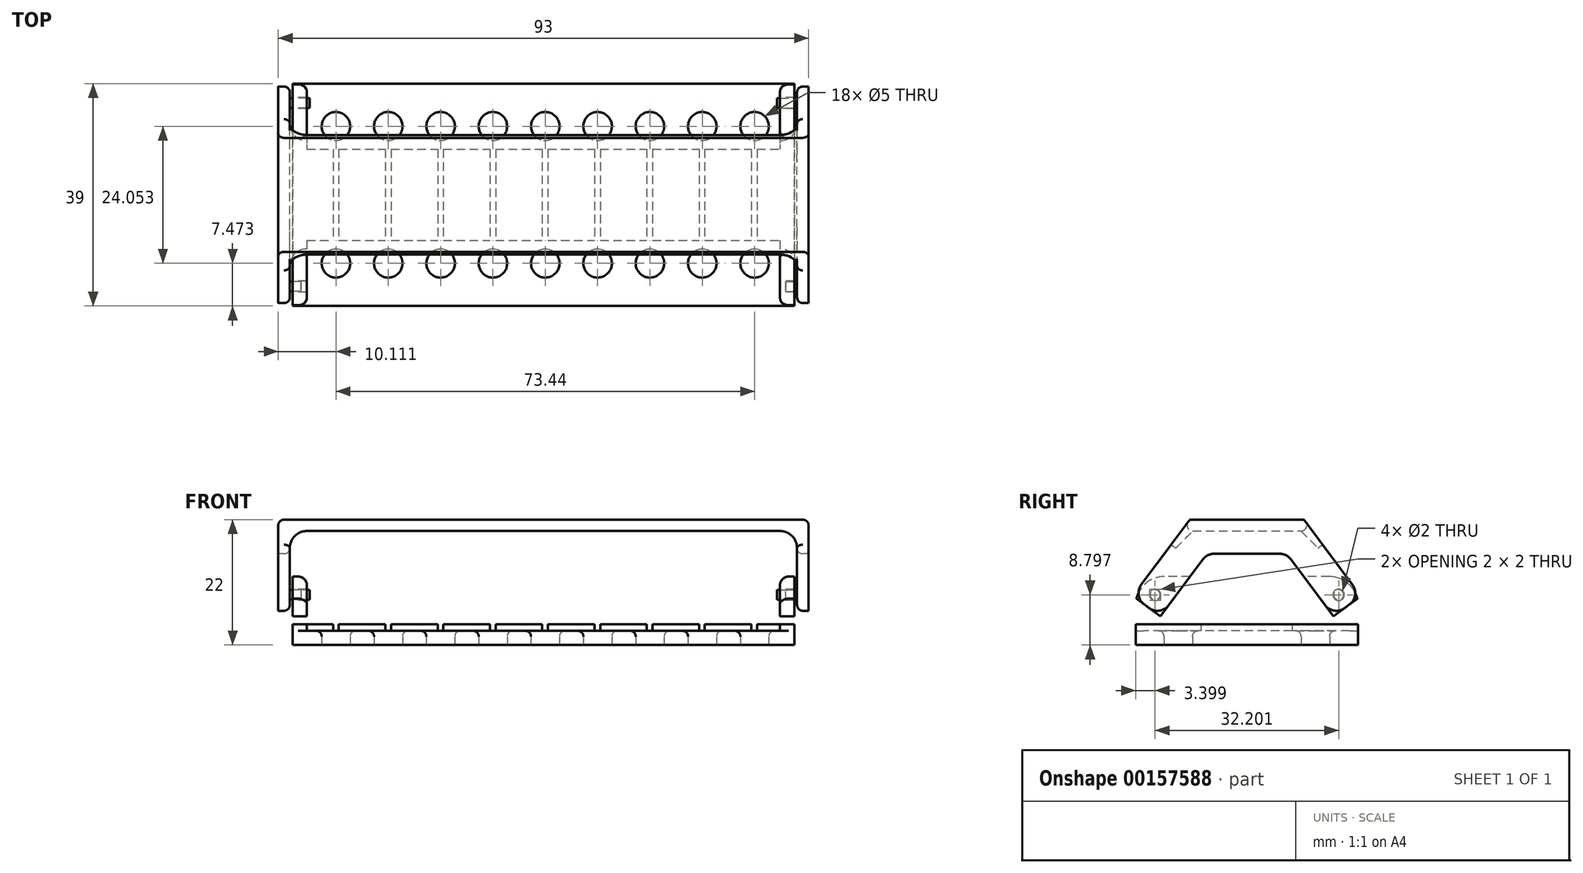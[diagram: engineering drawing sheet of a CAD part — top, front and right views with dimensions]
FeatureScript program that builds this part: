
annotation { "Feature Type Name" : "Feature", "Feature Type Description" : "" }
export const myFeature = defineFeature(function(context is Context, id is Id, definition is map)
    precondition{}
    {
        {
            var Q0;
            Q0=qCreatedBy(makeId("Top.planeOp"),FACE);
            var sketch = newSketch(context, id + "F0", { "sketchPlane" : qUnion([Q0])});
            skLineSegment(sketch, "E0.bottom", {"start": v(-44, 19.5) * mm, "end": v(44, 19.5) * mm});
            skLineSegment(sketch, "E0.top", {"start": v(-44, -19.5) * mm, "end": v(44, -19.5) * mm});
            skLineSegment(sketch, "E0.left", {"start": v(-44, 19.5) * mm, "end": v(-44, -19.5) * mm});
            skLineSegment(sketch, "E0.right", {"start": v(44, 19.5) * mm, "end": v(44, -19.5) * mm});
            skLineSegment(sketch, "E1", {"start": v(-44, 0) * mm, "end": v(44, 0) * mm, "construction": true});
            skSolve(sketch);
        }
        {
            var Q0;
            Q0=makeQuery(id+"F0.imprint","IMPRINT",FACE,{"disambiguationData":[TD([[makeQuery(id+"F0.imprint","IMPRINT",EDGE,{"derivedFrom":sQuery(id+"F0.wireOp",EDGE,"E0.bottom")}),-1.0]])]});
            var Q1;
            Q1=sQuery(id+"F0.wireOp",EDGE,"E0.top");
            extrude(context, id + "F1", {"entities" : qUnion([Q0]), "surfaceEntities" : qUnion([Q1]), "depth" : 12 * mm});
        }
        {
            var Q0;
            Q0=qCreatedBy(makeId("Top.planeOp"),FACE);
            cPlane(context, id + "F2", {"entities" : qUnion([Q0]), "cplaneType" : CPlaneType.OFFSET, "offset" : 12 * mm, "width" : 150 * mm, "height" : 150 * mm});
        }
        {
            var Q0;
            Q0=qCreatedBy(id+"F2.planeOp",FACE);
            var sketch = newSketch(context, id + "F3", { "sketchPlane" : qUnion([Q0])});
            skLineSegment(sketch, "E2.bottom", {"start": v(-41.5, 19.5) * mm, "end": v(41.5, 19.5) * mm});
            skLineSegment(sketch, "E2.top", {"start": v(-41.5, 8) * mm, "end": v(41.5, 8) * mm});
            skLineSegment(sketch, "E2.left", {"start": v(-41.5, 19.5) * mm, "end": v(-41.5, 8) * mm});
            skLineSegment(sketch, "E2.right", {"start": v(41.5, 19.5) * mm, "end": v(41.5, 8) * mm});
            skLineSegment(sketch, "E3.bottom", {"start": v(-41.5, -8) * mm, "end": v(41.5, -8) * mm});
            skLineSegment(sketch, "E3.top", {"start": v(-41.5, -19.5) * mm, "end": v(41.5, -19.5) * mm});
            skLineSegment(sketch, "E3.left", {"start": v(-41.5, -8) * mm, "end": v(-41.5, -19.5) * mm});
            skLineSegment(sketch, "E3.right", {"start": v(41.5, -8) * mm, "end": v(41.5, -19.5) * mm});
            skLineSegment(sketch, "E4", {"start": v(0, 8) * mm, "end": v(0, -8) * mm, "construction": true});
            skSolve(sketch);
        }
        {
            var Q0;
            Q0 = qSketchRegion(id + "F3", true);
            extrude(context, id + "F4", {"entities" : qUnion([Q0]), "operationType" : NewBodyOperationType.REMOVE, "oppositeDirection" : true, "depth" : 9.5 * mm});
        }
        {
            var Q0;
            Q0=qCreatedBy(id+"F2.planeOp",FACE);
            var sketch = newSketch(context, id + "F5", { "sketchPlane" : qUnion([Q0])});
            skLineSegment(sketch, "E5.bottom", {"start": v(-36.89, 8) * mm, "end": v(-35.89, 8) * mm});
            skLineSegment(sketch, "E5.top", {"start": v(-36.89, -8) * mm, "end": v(-35.89, -8) * mm});
            skLineSegment(sketch, "E5.left", {"start": v(-36.89, 8) * mm, "end": v(-36.89, -8) * mm});
            skLineSegment(sketch, "E5.right", {"start": v(-35.89, 8) * mm, "end": v(-35.89, -8) * mm});
            skLineSegment(sketch, "E6.1.0.0", {"start": v(-27.72, 8) * mm, "end": v(-26.72, 8) * mm});
            skLineSegment(sketch, "E6.1.0.1", {"start": v(-26.72, 8) * mm, "end": v(-26.72, -8) * mm});
            skLineSegment(sketch, "E6.1.0.2", {"start": v(-27.72, -8) * mm, "end": v(-26.72, -8) * mm});
            skLineSegment(sketch, "E6.1.0.3", {"start": v(-27.72, 8) * mm, "end": v(-27.72, -8) * mm});
            skLineSegment(sketch, "E6.2.0.0", {"start": v(-18.55, 8) * mm, "end": v(-17.55, 8) * mm});
            skLineSegment(sketch, "E6.2.0.1", {"start": v(-17.55, 8) * mm, "end": v(-17.55, -8) * mm});
            skLineSegment(sketch, "E6.2.0.2", {"start": v(-18.55, -8) * mm, "end": v(-17.55, -8) * mm});
            skLineSegment(sketch, "E6.2.0.3", {"start": v(-18.55, 8) * mm, "end": v(-18.55, -8) * mm});
            skLineSegment(sketch, "E6.3.0.0", {"start": v(-9.38, 8) * mm, "end": v(-8.38, 8) * mm});
            skLineSegment(sketch, "E6.3.0.1", {"start": v(-8.38, 8) * mm, "end": v(-8.38, -8) * mm});
            skLineSegment(sketch, "E6.3.0.2", {"start": v(-9.38, -8) * mm, "end": v(-8.38, -8) * mm});
            skLineSegment(sketch, "E6.3.0.3", {"start": v(-9.38, 8) * mm, "end": v(-9.38, -8) * mm});
            skLineSegment(sketch, "E6.4.0.0", {"start": v(-0.2, 8) * mm, "end": v(0.8, 8) * mm});
            skLineSegment(sketch, "E6.4.0.1", {"start": v(0.8, 8) * mm, "end": v(0.8, -8) * mm});
            skLineSegment(sketch, "E6.4.0.2", {"start": v(-0.2, -8) * mm, "end": v(0.8, -8) * mm});
            skLineSegment(sketch, "E6.4.0.3", {"start": v(-0.2, 8) * mm, "end": v(-0.2, -8) * mm});
            skLineSegment(sketch, "E6.5.0.0", {"start": v(8.96, 8) * mm, "end": v(9.96, 8) * mm});
            skLineSegment(sketch, "E6.5.0.1", {"start": v(9.96, 8) * mm, "end": v(9.96, -8) * mm});
            skLineSegment(sketch, "E6.5.0.2", {"start": v(8.96, -8) * mm, "end": v(9.96, -8) * mm});
            skLineSegment(sketch, "E6.5.0.3", {"start": v(8.96, 8) * mm, "end": v(8.96, -8) * mm});
            skLineSegment(sketch, "E6.6.0.0", {"start": v(18.13, 8) * mm, "end": v(19.13, 8) * mm});
            skLineSegment(sketch, "E6.6.0.1", {"start": v(19.13, 8) * mm, "end": v(19.13, -8) * mm});
            skLineSegment(sketch, "E6.6.0.2", {"start": v(18.13, -8) * mm, "end": v(19.13, -8) * mm});
            skLineSegment(sketch, "E6.6.0.3", {"start": v(18.13, 8) * mm, "end": v(18.13, -8) * mm});
            skLineSegment(sketch, "E6.7.0.0", {"start": v(27.3, 8) * mm, "end": v(28.3, 8) * mm});
            skLineSegment(sketch, "E6.7.0.1", {"start": v(28.3, 8) * mm, "end": v(28.3, -8) * mm});
            skLineSegment(sketch, "E6.7.0.2", {"start": v(27.3, -8) * mm, "end": v(28.3, -8) * mm});
            skLineSegment(sketch, "E6.7.0.3", {"start": v(27.3, 8) * mm, "end": v(27.3, -8) * mm});
            skLineSegment(sketch, "E6.8.0.0", {"start": v(36.47, 8) * mm, "end": v(37.47, 8) * mm});
            skLineSegment(sketch, "E6.8.0.1", {"start": v(37.47, 8) * mm, "end": v(37.47, -8) * mm});
            skLineSegment(sketch, "E6.8.0.2", {"start": v(36.47, -8) * mm, "end": v(37.47, -8) * mm});
            skLineSegment(sketch, "E6.8.0.3", {"start": v(36.47, 8) * mm, "end": v(36.47, -8) * mm});
            skLineSegment(sketch, "E6.direction1", {"start": v(-36.89, 8) * mm, "end": v(-27.72, 8) * mm, "construction": true});
            skSolve(sketch);
        }
        {
            var Q0;
            Q0=qCreatedBy(id+"F2.planeOp",FACE);
            var sketch = newSketch(context, id + "F6", { "sketchPlane" : qUnion([Q0])});
            skLineSegment(sketch, "E7.bottom", {"start": v(-41.5, 8) * mm, "end": v(41.5, 8) * mm});
            skLineSegment(sketch, "E7.top", {"start": v(-41.5, -8) * mm, "end": v(41.5, -8) * mm});
            skLineSegment(sketch, "E7.left", {"start": v(-41.5, 8) * mm, "end": v(-41.5, -8) * mm});
            skLineSegment(sketch, "E7.right", {"start": v(41.5, 8) * mm, "end": v(41.5, -8) * mm});
            skSolve(sketch);
        }
        {
            var Q0;
            Q0 = qSketchRegion(id + "F6", true);
            extrude(context, id + "F7", {"entities" : qUnion([Q0]), "operationType" : NewBodyOperationType.REMOVE, "oppositeDirection" : true, "depth" : 2 * mm});
        }
        {
            var Q0;
            Q0 = qSketchRegion(id + "F5", true);
            extrude(context, id + "F8", {"entities" : qUnion([Q0]), "operationType" : NewBodyOperationType.REMOVE, "oppositeDirection" : true, "depth" : 9.5 * mm});
        }
        {
            var Q0;
            {var subQ0=sQuery(id+"F0.wireOp",EDGE,"E0.left");var subQ1=sQuery(id+"F0.wireOp",EDGE,"E0.top");Q0=makeQuery(id+"F4.boolean.opBoolean","SPLIT",EDGE,{"disambiguationData":[TD([makeQuery(id+"F1.opExtrude","SWEPT_FACE",FACE,{"disambiguationData":[OSD([subQ0])]})])],"derivedFrom":makeQuery(id+"F1.opExtrude","CAP_EDGE",EDGE,{"disambiguationData":[OSD([subQ1])],"isStart":false})});}
            var Q1;
            {var subQ0=sQuery(id+"F0.wireOp",EDGE,"E0.bottom");var subQ1=sQuery(id+"F0.wireOp",EDGE,"E0.left");Q1=makeQuery(id+"F4.boolean.opBoolean","SPLIT",EDGE,{"disambiguationData":[TD([makeQuery(id+"F1.opExtrude","SWEPT_FACE",FACE,{"disambiguationData":[OSD([subQ1])]})])],"derivedFrom":makeQuery(id+"F1.opExtrude","CAP_EDGE",EDGE,{"disambiguationData":[OSD([subQ0])],"isStart":false})});}
            var Q2;
            {var subQ0=sQuery(id+"F0.wireOp",EDGE,"E0.right");var subQ1=sQuery(id+"F0.wireOp",EDGE,"E0.top");Q2=makeQuery(id+"F4.boolean.opBoolean","SPLIT",EDGE,{"disambiguationData":[TD([makeQuery(id+"F1.opExtrude","SWEPT_FACE",FACE,{"disambiguationData":[OSD([subQ0])]})])],"derivedFrom":makeQuery(id+"F1.opExtrude","CAP_EDGE",EDGE,{"disambiguationData":[OSD([subQ1])],"isStart":false})});}
            var Q3;
            {var subQ0=sQuery(id+"F0.wireOp",EDGE,"E0.bottom");var subQ1=sQuery(id+"F0.wireOp",EDGE,"E0.right");Q3=makeQuery(id+"F4.boolean.opBoolean","SPLIT",EDGE,{"disambiguationData":[TD([makeQuery(id+"F1.opExtrude","SWEPT_FACE",FACE,{"disambiguationData":[OSD([subQ1])]})])],"derivedFrom":makeQuery(id+"F1.opExtrude","CAP_EDGE",EDGE,{"disambiguationData":[OSD([subQ0])],"isStart":false})});}
            fillet(context, id + "F9", {"entities" : qUnion([Q0, Q1, Q2, Q3]), "radius" : 5 * mm, "tangentPropagation" : true, "allowEdgeOverflow" : false});
        }
        {
            var Q0;
            {var subQ0=makeQuery(id+"F4.opExtrude","SWEPT_FACE",FACE,{"disambiguationData":[OSD([sQuery(id+"F3.wireOp",EDGE,"E3.left")])]});var subQ1=sQuery(id+"F0.wireOp",EDGE,"E0.left");var subQ2=sQuery(id+"F0.wireOp",EDGE,"E0.top");Q0=makeQuery(id+"F9.opFillet","BLEND_EDGE",EDGE,{"blendedFrom":[makeQuery(id+"F4.boolean.opBoolean","SPLIT",EDGE,{"disambiguationData":[TD([makeQuery(id+"F1.opExtrude","SWEPT_FACE",FACE,{"disambiguationData":[OSD([subQ1])]})])],"derivedFrom":makeQuery(id+"F1.opExtrude","CAP_EDGE",EDGE,{"disambiguationData":[OSD([subQ2])],"isStart":false})}),makeQuery(id+"F7.boolean.opBoolean","MERGE",FACE,{"derivedFrom":[makeQuery(id+"F4.boolean.opBoolean","COPY",FACE,{"derivedFrom":makeQuery(id+"F4.opExtrude","SWEPT_FACE",FACE,{"disambiguationData":[OSD([sQuery(id+"F3.wireOp",EDGE,"E2.left")])]})}),makeQuery(id+"F4.boolean.opBoolean","COPY",FACE,{"derivedFrom":subQ0}),makeQuery(id+"F7.opExtrude","SWEPT_FACE",FACE,{"disambiguationData":[OSD([sQuery(id+"F6.wireOp",EDGE,"E7.left")])]})]})],"blendedInto":[makeQuery(id+"F7.boolean.opBoolean","MERGE",FACE,{"derivedFrom":[makeQuery(id+"F4.boolean.opBoolean","COPY",FACE,{"derivedFrom":makeQuery(id+"F4.opExtrude","SWEPT_FACE",FACE,{"disambiguationData":[OSD([sQuery(id+"F3.wireOp",EDGE,"E2.left")])]})}),makeQuery(id+"F4.boolean.opBoolean","COPY",FACE,{"derivedFrom":subQ0}),makeQuery(id+"F7.opExtrude","SWEPT_FACE",FACE,{"disambiguationData":[OSD([sQuery(id+"F6.wireOp",EDGE,"E7.left")])]})]})]});}
            var Q1;
            Q1=makeQuery(id+"F4.boolean.opBoolean","COPY",EDGE,{"derivedFrom":makeQuery(id+"F4.opExtrude","CAP_EDGE",EDGE,{"disambiguationData":[OSD([sQuery(id+"F3.wireOp",EDGE,"E3.top")])],"isStart":false})});
            var Q2;
            {var subQ0=makeQuery(id+"F4.opExtrude","SWEPT_FACE",FACE,{"disambiguationData":[OSD([sQuery(id+"F3.wireOp",EDGE,"E3.right")])]});var subQ1=sQuery(id+"F0.wireOp",EDGE,"E0.right");var subQ2=sQuery(id+"F0.wireOp",EDGE,"E0.top");Q2=makeQuery(id+"F9.opFillet","BLEND_EDGE",EDGE,{"blendedFrom":[makeQuery(id+"F4.boolean.opBoolean","SPLIT",EDGE,{"disambiguationData":[TD([makeQuery(id+"F1.opExtrude","SWEPT_FACE",FACE,{"disambiguationData":[OSD([subQ1])]})])],"derivedFrom":makeQuery(id+"F1.opExtrude","CAP_EDGE",EDGE,{"disambiguationData":[OSD([subQ2])],"isStart":false})}),makeQuery(id+"F7.boolean.opBoolean","MERGE",FACE,{"derivedFrom":[makeQuery(id+"F4.boolean.opBoolean","COPY",FACE,{"derivedFrom":makeQuery(id+"F4.opExtrude","SWEPT_FACE",FACE,{"disambiguationData":[OSD([sQuery(id+"F3.wireOp",EDGE,"E2.right")])]})}),makeQuery(id+"F4.boolean.opBoolean","COPY",FACE,{"derivedFrom":subQ0}),makeQuery(id+"F7.opExtrude","SWEPT_FACE",FACE,{"disambiguationData":[OSD([sQuery(id+"F6.wireOp",EDGE,"E7.right")])]})]})],"blendedInto":[makeQuery(id+"F7.boolean.opBoolean","MERGE",FACE,{"derivedFrom":[makeQuery(id+"F4.boolean.opBoolean","COPY",FACE,{"derivedFrom":makeQuery(id+"F4.opExtrude","SWEPT_FACE",FACE,{"disambiguationData":[OSD([sQuery(id+"F3.wireOp",EDGE,"E2.right")])]})}),makeQuery(id+"F4.boolean.opBoolean","COPY",FACE,{"derivedFrom":subQ0}),makeQuery(id+"F7.opExtrude","SWEPT_FACE",FACE,{"disambiguationData":[OSD([sQuery(id+"F6.wireOp",EDGE,"E7.right")])]})]})]});}
            var Q3;
            Q3=makeQuery(id+"F4.boolean.opBoolean","COPY",EDGE,{"derivedFrom":makeQuery(id+"F4.opExtrude","CAP_EDGE",EDGE,{"disambiguationData":[OSD([sQuery(id+"F3.wireOp",EDGE,"E2.bottom")])],"isStart":false})});
            fillet(context, id + "F10", {"entities" : qUnion([Q0, Q1, Q2, Q3]), "radius" : 1.5 * mm, "tangentPropagation" : true, "allowEdgeOverflow" : false});
        }
        {
            var Q0;
            Q0=qCreatedBy(makeId("Top.planeOp"),FACE);
            var sketch = newSketch(context, id + "F11", { "sketchPlane" : qUnion([Q0])});
            skCircle(sketch, "E8", {"center": v(-36.39, 12.03) * mm, "radius": 2.5 * mm});
            skLineSegment(sketch, "E9", {"start": v(-36.39, 12.03) * mm, "end": v(-36.39, 7.94) * mm});
            skCircle(sketch, "E10.1.0.0", {"center": v(-27.2, 12.03) * mm, "radius": 2.5 * mm});
            skCircle(sketch, "E10.2.0.0", {"center": v(-18.03, 12.03) * mm, "radius": 2.5 * mm});
            skCircle(sketch, "E10.3.0.0", {"center": v(-8.85, 12.03) * mm, "radius": 2.5 * mm});
            skCircle(sketch, "E10.4.0.0", {"center": v(0.33, 12.03) * mm, "radius": 2.5 * mm});
            skCircle(sketch, "E10.5.0.0", {"center": v(9.51, 12.03) * mm, "radius": 2.5 * mm});
            skCircle(sketch, "E10.6.0.0", {"center": v(18.7, 12.03) * mm, "radius": 2.5 * mm});
            skCircle(sketch, "E10.7.0.0", {"center": v(27.87, 12.03) * mm, "radius": 2.5 * mm});
            skCircle(sketch, "E10.8.0.0", {"center": v(37.05, 12.03) * mm, "radius": 2.5 * mm});
            skLineSegment(sketch, "E10.direction1", {"start": v(-36.39, 12.03) * mm, "end": v(-27.2, 12.03) * mm, "construction": true});
            skLineSegment(sketch, "E11", {"start": v(-41.42, 0) * mm, "end": v(0, 0) * mm, "construction": true});
            skCircle(sketch, "E12.MirrorC", {"center": v(-36.39, -12.03) * mm, "radius": 2.5 * mm});
            skCircle(sketch, "E13.MirrorC", {"center": v(-27.2, -12.03) * mm, "radius": 2.5 * mm});
            skCircle(sketch, "E14.MirrorC", {"center": v(-18.03, -12.03) * mm, "radius": 2.5 * mm});
            skCircle(sketch, "E15.MirrorC", {"center": v(-8.85, -12.03) * mm, "radius": 2.5 * mm});
            skCircle(sketch, "E16.MirrorC", {"center": v(0.33, -12.03) * mm, "radius": 2.5 * mm});
            skCircle(sketch, "E17.MirrorC", {"center": v(9.51, -12.03) * mm, "radius": 2.5 * mm});
            skCircle(sketch, "E18.MirrorC", {"center": v(18.7, -12.03) * mm, "radius": 2.5 * mm});
            skCircle(sketch, "E19.MirrorC", {"center": v(27.87, -12.03) * mm, "radius": 2.5 * mm});
            skCircle(sketch, "E20.MirrorC", {"center": v(37.05, -12.03) * mm, "radius": 2.5 * mm});
            skSolve(sketch);
        }
        {
            var Q0;
            Q0 = qSketchRegion(id + "F11", true);
            extrude(context, id + "F12", {"entities" : qUnion([Q0]), "operationType" : NewBodyOperationType.REMOVE, "depth" : 25 * mm});
        }
        {
            var Q0;
            Q0=makeQuery(id+"F12.boolean.opBoolean","INTERSECT",EDGE,{"derivedFrom":[makeQuery(id+"F8.boolean.opBoolean","MERGE",FACE,{"derivedFrom":[makeQuery(id+"F4.boolean.opBoolean","COPY",FACE,{"derivedFrom":makeQuery(id+"F4.opExtrude","CAP_FACE",FACE,{"disambiguationData":[OSD([sQuery(id+"F3.wireOp",EDGE,"E2.bottom"),sQuery(id+"F3.wireOp",EDGE,"E2.top"),sQuery(id+"F3.wireOp",EDGE,"E2.left"),sQuery(id+"F3.wireOp",EDGE,"E2.right")])],"isStart":false})}),makeQuery(id+"F4.boolean.opBoolean","COPY",FACE,{"derivedFrom":makeQuery(id+"F4.opExtrude","CAP_FACE",FACE,{"disambiguationData":[OSD([sQuery(id+"F3.wireOp",EDGE,"E3.bottom"),sQuery(id+"F3.wireOp",EDGE,"E3.top"),sQuery(id+"F3.wireOp",EDGE,"E3.left"),sQuery(id+"F3.wireOp",EDGE,"E3.right")])],"isStart":false})}),makeQuery(id+"F8.opExtrude","CAP_FACE",FACE,{"disambiguationData":[OSD([sQuery(id+"F5.wireOp",EDGE,"E5.bottom"),sQuery(id+"F5.wireOp",EDGE,"E5.top"),sQuery(id+"F5.wireOp",EDGE,"E5.left"),sQuery(id+"F5.wireOp",EDGE,"E5.right")])],"isStart":false}),makeQuery(id+"F8.opExtrude","CAP_FACE",FACE,{"disambiguationData":[OSD([sQuery(id+"F5.wireOp",EDGE,"E6.1.0.0"),sQuery(id+"F5.wireOp",EDGE,"E6.1.0.1"),sQuery(id+"F5.wireOp",EDGE,"E6.1.0.2"),sQuery(id+"F5.wireOp",EDGE,"E6.1.0.3")])],"isStart":false}),makeQuery(id+"F8.opExtrude","CAP_FACE",FACE,{"disambiguationData":[OSD([sQuery(id+"F5.wireOp",EDGE,"E6.2.0.0"),sQuery(id+"F5.wireOp",EDGE,"E6.2.0.1"),sQuery(id+"F5.wireOp",EDGE,"E6.2.0.2"),sQuery(id+"F5.wireOp",EDGE,"E6.2.0.3")])],"isStart":false}),makeQuery(id+"F8.opExtrude","CAP_FACE",FACE,{"disambiguationData":[OSD([sQuery(id+"F5.wireOp",EDGE,"E6.3.0.0"),sQuery(id+"F5.wireOp",EDGE,"E6.3.0.1"),sQuery(id+"F5.wireOp",EDGE,"E6.3.0.2"),sQuery(id+"F5.wireOp",EDGE,"E6.3.0.3")])],"isStart":false}),makeQuery(id+"F8.opExtrude","CAP_FACE",FACE,{"disambiguationData":[OSD([sQuery(id+"F5.wireOp",EDGE,"E6.4.0.0"),sQuery(id+"F5.wireOp",EDGE,"E6.4.0.1"),sQuery(id+"F5.wireOp",EDGE,"E6.4.0.2"),sQuery(id+"F5.wireOp",EDGE,"E6.4.0.3")])],"isStart":false}),makeQuery(id+"F8.opExtrude","CAP_FACE",FACE,{"disambiguationData":[OSD([sQuery(id+"F5.wireOp",EDGE,"E6.5.0.0"),sQuery(id+"F5.wireOp",EDGE,"E6.5.0.1"),sQuery(id+"F5.wireOp",EDGE,"E6.5.0.2"),sQuery(id+"F5.wireOp",EDGE,"E6.5.0.3")])],"isStart":false}),makeQuery(id+"F8.opExtrude","CAP_FACE",FACE,{"disambiguationData":[OSD([sQuery(id+"F5.wireOp",EDGE,"E6.6.0.0"),sQuery(id+"F5.wireOp",EDGE,"E6.6.0.1"),sQuery(id+"F5.wireOp",EDGE,"E6.6.0.2"),sQuery(id+"F5.wireOp",EDGE,"E6.6.0.3")])],"isStart":false}),makeQuery(id+"F8.opExtrude","CAP_FACE",FACE,{"disambiguationData":[OSD([sQuery(id+"F5.wireOp",EDGE,"E6.7.0.0"),sQuery(id+"F5.wireOp",EDGE,"E6.7.0.1"),sQuery(id+"F5.wireOp",EDGE,"E6.7.0.2"),sQuery(id+"F5.wireOp",EDGE,"E6.7.0.3")])],"isStart":false}),makeQuery(id+"F8.opExtrude","CAP_FACE",FACE,{"disambiguationData":[OSD([sQuery(id+"F5.wireOp",EDGE,"E6.8.0.0"),sQuery(id+"F5.wireOp",EDGE,"E6.8.0.1"),sQuery(id+"F5.wireOp",EDGE,"E6.8.0.2"),sQuery(id+"F5.wireOp",EDGE,"E6.8.0.3")])],"isStart":false})]}),makeQuery(id+"F12.opExtrude","SWEPT_FACE",FACE,{"disambiguationData":[OSD([sQuery(id+"F11.wireOp",EDGE,"E12.MirrorC")])]})]});
            var Q1;
            Q1=makeQuery(id+"F12.boolean.opBoolean","INTERSECT",EDGE,{"derivedFrom":[makeQuery(id+"F8.boolean.opBoolean","MERGE",FACE,{"derivedFrom":[makeQuery(id+"F4.boolean.opBoolean","COPY",FACE,{"derivedFrom":makeQuery(id+"F4.opExtrude","CAP_FACE",FACE,{"disambiguationData":[OSD([sQuery(id+"F3.wireOp",EDGE,"E2.bottom"),sQuery(id+"F3.wireOp",EDGE,"E2.top"),sQuery(id+"F3.wireOp",EDGE,"E2.left"),sQuery(id+"F3.wireOp",EDGE,"E2.right")])],"isStart":false})}),makeQuery(id+"F4.boolean.opBoolean","COPY",FACE,{"derivedFrom":makeQuery(id+"F4.opExtrude","CAP_FACE",FACE,{"disambiguationData":[OSD([sQuery(id+"F3.wireOp",EDGE,"E3.bottom"),sQuery(id+"F3.wireOp",EDGE,"E3.top"),sQuery(id+"F3.wireOp",EDGE,"E3.left"),sQuery(id+"F3.wireOp",EDGE,"E3.right")])],"isStart":false})}),makeQuery(id+"F8.opExtrude","CAP_FACE",FACE,{"disambiguationData":[OSD([sQuery(id+"F5.wireOp",EDGE,"E5.bottom"),sQuery(id+"F5.wireOp",EDGE,"E5.top"),sQuery(id+"F5.wireOp",EDGE,"E5.left"),sQuery(id+"F5.wireOp",EDGE,"E5.right")])],"isStart":false}),makeQuery(id+"F8.opExtrude","CAP_FACE",FACE,{"disambiguationData":[OSD([sQuery(id+"F5.wireOp",EDGE,"E6.1.0.0"),sQuery(id+"F5.wireOp",EDGE,"E6.1.0.1"),sQuery(id+"F5.wireOp",EDGE,"E6.1.0.2"),sQuery(id+"F5.wireOp",EDGE,"E6.1.0.3")])],"isStart":false}),makeQuery(id+"F8.opExtrude","CAP_FACE",FACE,{"disambiguationData":[OSD([sQuery(id+"F5.wireOp",EDGE,"E6.2.0.0"),sQuery(id+"F5.wireOp",EDGE,"E6.2.0.1"),sQuery(id+"F5.wireOp",EDGE,"E6.2.0.2"),sQuery(id+"F5.wireOp",EDGE,"E6.2.0.3")])],"isStart":false}),makeQuery(id+"F8.opExtrude","CAP_FACE",FACE,{"disambiguationData":[OSD([sQuery(id+"F5.wireOp",EDGE,"E6.3.0.0"),sQuery(id+"F5.wireOp",EDGE,"E6.3.0.1"),sQuery(id+"F5.wireOp",EDGE,"E6.3.0.2"),sQuery(id+"F5.wireOp",EDGE,"E6.3.0.3")])],"isStart":false}),makeQuery(id+"F8.opExtrude","CAP_FACE",FACE,{"disambiguationData":[OSD([sQuery(id+"F5.wireOp",EDGE,"E6.4.0.0"),sQuery(id+"F5.wireOp",EDGE,"E6.4.0.1"),sQuery(id+"F5.wireOp",EDGE,"E6.4.0.2"),sQuery(id+"F5.wireOp",EDGE,"E6.4.0.3")])],"isStart":false}),makeQuery(id+"F8.opExtrude","CAP_FACE",FACE,{"disambiguationData":[OSD([sQuery(id+"F5.wireOp",EDGE,"E6.5.0.0"),sQuery(id+"F5.wireOp",EDGE,"E6.5.0.1"),sQuery(id+"F5.wireOp",EDGE,"E6.5.0.2"),sQuery(id+"F5.wireOp",EDGE,"E6.5.0.3")])],"isStart":false}),makeQuery(id+"F8.opExtrude","CAP_FACE",FACE,{"disambiguationData":[OSD([sQuery(id+"F5.wireOp",EDGE,"E6.6.0.0"),sQuery(id+"F5.wireOp",EDGE,"E6.6.0.1"),sQuery(id+"F5.wireOp",EDGE,"E6.6.0.2"),sQuery(id+"F5.wireOp",EDGE,"E6.6.0.3")])],"isStart":false}),makeQuery(id+"F8.opExtrude","CAP_FACE",FACE,{"disambiguationData":[OSD([sQuery(id+"F5.wireOp",EDGE,"E6.7.0.0"),sQuery(id+"F5.wireOp",EDGE,"E6.7.0.1"),sQuery(id+"F5.wireOp",EDGE,"E6.7.0.2"),sQuery(id+"F5.wireOp",EDGE,"E6.7.0.3")])],"isStart":false}),makeQuery(id+"F8.opExtrude","CAP_FACE",FACE,{"disambiguationData":[OSD([sQuery(id+"F5.wireOp",EDGE,"E6.8.0.0"),sQuery(id+"F5.wireOp",EDGE,"E6.8.0.1"),sQuery(id+"F5.wireOp",EDGE,"E6.8.0.2"),sQuery(id+"F5.wireOp",EDGE,"E6.8.0.3")])],"isStart":false})]}),makeQuery(id+"F12.opExtrude","SWEPT_FACE",FACE,{"disambiguationData":[OSD([sQuery(id+"F11.wireOp",EDGE,"E13.MirrorC")])]})]});
            var Q2;
            Q2=makeQuery(id+"F12.boolean.opBoolean","INTERSECT",EDGE,{"derivedFrom":[makeQuery(id+"F8.boolean.opBoolean","MERGE",FACE,{"derivedFrom":[makeQuery(id+"F4.boolean.opBoolean","COPY",FACE,{"derivedFrom":makeQuery(id+"F4.opExtrude","CAP_FACE",FACE,{"disambiguationData":[OSD([sQuery(id+"F3.wireOp",EDGE,"E2.bottom"),sQuery(id+"F3.wireOp",EDGE,"E2.top"),sQuery(id+"F3.wireOp",EDGE,"E2.left"),sQuery(id+"F3.wireOp",EDGE,"E2.right")])],"isStart":false})}),makeQuery(id+"F4.boolean.opBoolean","COPY",FACE,{"derivedFrom":makeQuery(id+"F4.opExtrude","CAP_FACE",FACE,{"disambiguationData":[OSD([sQuery(id+"F3.wireOp",EDGE,"E3.bottom"),sQuery(id+"F3.wireOp",EDGE,"E3.top"),sQuery(id+"F3.wireOp",EDGE,"E3.left"),sQuery(id+"F3.wireOp",EDGE,"E3.right")])],"isStart":false})}),makeQuery(id+"F8.opExtrude","CAP_FACE",FACE,{"disambiguationData":[OSD([sQuery(id+"F5.wireOp",EDGE,"E5.bottom"),sQuery(id+"F5.wireOp",EDGE,"E5.top"),sQuery(id+"F5.wireOp",EDGE,"E5.left"),sQuery(id+"F5.wireOp",EDGE,"E5.right")])],"isStart":false}),makeQuery(id+"F8.opExtrude","CAP_FACE",FACE,{"disambiguationData":[OSD([sQuery(id+"F5.wireOp",EDGE,"E6.1.0.0"),sQuery(id+"F5.wireOp",EDGE,"E6.1.0.1"),sQuery(id+"F5.wireOp",EDGE,"E6.1.0.2"),sQuery(id+"F5.wireOp",EDGE,"E6.1.0.3")])],"isStart":false}),makeQuery(id+"F8.opExtrude","CAP_FACE",FACE,{"disambiguationData":[OSD([sQuery(id+"F5.wireOp",EDGE,"E6.2.0.0"),sQuery(id+"F5.wireOp",EDGE,"E6.2.0.1"),sQuery(id+"F5.wireOp",EDGE,"E6.2.0.2"),sQuery(id+"F5.wireOp",EDGE,"E6.2.0.3")])],"isStart":false}),makeQuery(id+"F8.opExtrude","CAP_FACE",FACE,{"disambiguationData":[OSD([sQuery(id+"F5.wireOp",EDGE,"E6.3.0.0"),sQuery(id+"F5.wireOp",EDGE,"E6.3.0.1"),sQuery(id+"F5.wireOp",EDGE,"E6.3.0.2"),sQuery(id+"F5.wireOp",EDGE,"E6.3.0.3")])],"isStart":false}),makeQuery(id+"F8.opExtrude","CAP_FACE",FACE,{"disambiguationData":[OSD([sQuery(id+"F5.wireOp",EDGE,"E6.4.0.0"),sQuery(id+"F5.wireOp",EDGE,"E6.4.0.1"),sQuery(id+"F5.wireOp",EDGE,"E6.4.0.2"),sQuery(id+"F5.wireOp",EDGE,"E6.4.0.3")])],"isStart":false}),makeQuery(id+"F8.opExtrude","CAP_FACE",FACE,{"disambiguationData":[OSD([sQuery(id+"F5.wireOp",EDGE,"E6.5.0.0"),sQuery(id+"F5.wireOp",EDGE,"E6.5.0.1"),sQuery(id+"F5.wireOp",EDGE,"E6.5.0.2"),sQuery(id+"F5.wireOp",EDGE,"E6.5.0.3")])],"isStart":false}),makeQuery(id+"F8.opExtrude","CAP_FACE",FACE,{"disambiguationData":[OSD([sQuery(id+"F5.wireOp",EDGE,"E6.6.0.0"),sQuery(id+"F5.wireOp",EDGE,"E6.6.0.1"),sQuery(id+"F5.wireOp",EDGE,"E6.6.0.2"),sQuery(id+"F5.wireOp",EDGE,"E6.6.0.3")])],"isStart":false}),makeQuery(id+"F8.opExtrude","CAP_FACE",FACE,{"disambiguationData":[OSD([sQuery(id+"F5.wireOp",EDGE,"E6.7.0.0"),sQuery(id+"F5.wireOp",EDGE,"E6.7.0.1"),sQuery(id+"F5.wireOp",EDGE,"E6.7.0.2"),sQuery(id+"F5.wireOp",EDGE,"E6.7.0.3")])],"isStart":false}),makeQuery(id+"F8.opExtrude","CAP_FACE",FACE,{"disambiguationData":[OSD([sQuery(id+"F5.wireOp",EDGE,"E6.8.0.0"),sQuery(id+"F5.wireOp",EDGE,"E6.8.0.1"),sQuery(id+"F5.wireOp",EDGE,"E6.8.0.2"),sQuery(id+"F5.wireOp",EDGE,"E6.8.0.3")])],"isStart":false})]}),makeQuery(id+"F12.opExtrude","SWEPT_FACE",FACE,{"disambiguationData":[OSD([sQuery(id+"F11.wireOp",EDGE,"E14.MirrorC")])]})]});
            var Q3;
            Q3=makeQuery(id+"F12.boolean.opBoolean","INTERSECT",EDGE,{"derivedFrom":[makeQuery(id+"F8.boolean.opBoolean","MERGE",FACE,{"derivedFrom":[makeQuery(id+"F4.boolean.opBoolean","COPY",FACE,{"derivedFrom":makeQuery(id+"F4.opExtrude","CAP_FACE",FACE,{"disambiguationData":[OSD([sQuery(id+"F3.wireOp",EDGE,"E2.bottom"),sQuery(id+"F3.wireOp",EDGE,"E2.top"),sQuery(id+"F3.wireOp",EDGE,"E2.left"),sQuery(id+"F3.wireOp",EDGE,"E2.right")])],"isStart":false})}),makeQuery(id+"F4.boolean.opBoolean","COPY",FACE,{"derivedFrom":makeQuery(id+"F4.opExtrude","CAP_FACE",FACE,{"disambiguationData":[OSD([sQuery(id+"F3.wireOp",EDGE,"E3.bottom"),sQuery(id+"F3.wireOp",EDGE,"E3.top"),sQuery(id+"F3.wireOp",EDGE,"E3.left"),sQuery(id+"F3.wireOp",EDGE,"E3.right")])],"isStart":false})}),makeQuery(id+"F8.opExtrude","CAP_FACE",FACE,{"disambiguationData":[OSD([sQuery(id+"F5.wireOp",EDGE,"E5.bottom"),sQuery(id+"F5.wireOp",EDGE,"E5.top"),sQuery(id+"F5.wireOp",EDGE,"E5.left"),sQuery(id+"F5.wireOp",EDGE,"E5.right")])],"isStart":false}),makeQuery(id+"F8.opExtrude","CAP_FACE",FACE,{"disambiguationData":[OSD([sQuery(id+"F5.wireOp",EDGE,"E6.1.0.0"),sQuery(id+"F5.wireOp",EDGE,"E6.1.0.1"),sQuery(id+"F5.wireOp",EDGE,"E6.1.0.2"),sQuery(id+"F5.wireOp",EDGE,"E6.1.0.3")])],"isStart":false}),makeQuery(id+"F8.opExtrude","CAP_FACE",FACE,{"disambiguationData":[OSD([sQuery(id+"F5.wireOp",EDGE,"E6.2.0.0"),sQuery(id+"F5.wireOp",EDGE,"E6.2.0.1"),sQuery(id+"F5.wireOp",EDGE,"E6.2.0.2"),sQuery(id+"F5.wireOp",EDGE,"E6.2.0.3")])],"isStart":false}),makeQuery(id+"F8.opExtrude","CAP_FACE",FACE,{"disambiguationData":[OSD([sQuery(id+"F5.wireOp",EDGE,"E6.3.0.0"),sQuery(id+"F5.wireOp",EDGE,"E6.3.0.1"),sQuery(id+"F5.wireOp",EDGE,"E6.3.0.2"),sQuery(id+"F5.wireOp",EDGE,"E6.3.0.3")])],"isStart":false}),makeQuery(id+"F8.opExtrude","CAP_FACE",FACE,{"disambiguationData":[OSD([sQuery(id+"F5.wireOp",EDGE,"E6.4.0.0"),sQuery(id+"F5.wireOp",EDGE,"E6.4.0.1"),sQuery(id+"F5.wireOp",EDGE,"E6.4.0.2"),sQuery(id+"F5.wireOp",EDGE,"E6.4.0.3")])],"isStart":false}),makeQuery(id+"F8.opExtrude","CAP_FACE",FACE,{"disambiguationData":[OSD([sQuery(id+"F5.wireOp",EDGE,"E6.5.0.0"),sQuery(id+"F5.wireOp",EDGE,"E6.5.0.1"),sQuery(id+"F5.wireOp",EDGE,"E6.5.0.2"),sQuery(id+"F5.wireOp",EDGE,"E6.5.0.3")])],"isStart":false}),makeQuery(id+"F8.opExtrude","CAP_FACE",FACE,{"disambiguationData":[OSD([sQuery(id+"F5.wireOp",EDGE,"E6.6.0.0"),sQuery(id+"F5.wireOp",EDGE,"E6.6.0.1"),sQuery(id+"F5.wireOp",EDGE,"E6.6.0.2"),sQuery(id+"F5.wireOp",EDGE,"E6.6.0.3")])],"isStart":false}),makeQuery(id+"F8.opExtrude","CAP_FACE",FACE,{"disambiguationData":[OSD([sQuery(id+"F5.wireOp",EDGE,"E6.7.0.0"),sQuery(id+"F5.wireOp",EDGE,"E6.7.0.1"),sQuery(id+"F5.wireOp",EDGE,"E6.7.0.2"),sQuery(id+"F5.wireOp",EDGE,"E6.7.0.3")])],"isStart":false}),makeQuery(id+"F8.opExtrude","CAP_FACE",FACE,{"disambiguationData":[OSD([sQuery(id+"F5.wireOp",EDGE,"E6.8.0.0"),sQuery(id+"F5.wireOp",EDGE,"E6.8.0.1"),sQuery(id+"F5.wireOp",EDGE,"E6.8.0.2"),sQuery(id+"F5.wireOp",EDGE,"E6.8.0.3")])],"isStart":false})]}),makeQuery(id+"F12.opExtrude","SWEPT_FACE",FACE,{"disambiguationData":[OSD([sQuery(id+"F11.wireOp",EDGE,"E15.MirrorC")])]})]});
            var Q4;
            Q4=makeQuery(id+"F12.boolean.opBoolean","INTERSECT",EDGE,{"derivedFrom":[makeQuery(id+"F8.boolean.opBoolean","MERGE",FACE,{"derivedFrom":[makeQuery(id+"F4.boolean.opBoolean","COPY",FACE,{"derivedFrom":makeQuery(id+"F4.opExtrude","CAP_FACE",FACE,{"disambiguationData":[OSD([sQuery(id+"F3.wireOp",EDGE,"E2.bottom"),sQuery(id+"F3.wireOp",EDGE,"E2.top"),sQuery(id+"F3.wireOp",EDGE,"E2.left"),sQuery(id+"F3.wireOp",EDGE,"E2.right")])],"isStart":false})}),makeQuery(id+"F4.boolean.opBoolean","COPY",FACE,{"derivedFrom":makeQuery(id+"F4.opExtrude","CAP_FACE",FACE,{"disambiguationData":[OSD([sQuery(id+"F3.wireOp",EDGE,"E3.bottom"),sQuery(id+"F3.wireOp",EDGE,"E3.top"),sQuery(id+"F3.wireOp",EDGE,"E3.left"),sQuery(id+"F3.wireOp",EDGE,"E3.right")])],"isStart":false})}),makeQuery(id+"F8.opExtrude","CAP_FACE",FACE,{"disambiguationData":[OSD([sQuery(id+"F5.wireOp",EDGE,"E5.bottom"),sQuery(id+"F5.wireOp",EDGE,"E5.top"),sQuery(id+"F5.wireOp",EDGE,"E5.left"),sQuery(id+"F5.wireOp",EDGE,"E5.right")])],"isStart":false}),makeQuery(id+"F8.opExtrude","CAP_FACE",FACE,{"disambiguationData":[OSD([sQuery(id+"F5.wireOp",EDGE,"E6.1.0.0"),sQuery(id+"F5.wireOp",EDGE,"E6.1.0.1"),sQuery(id+"F5.wireOp",EDGE,"E6.1.0.2"),sQuery(id+"F5.wireOp",EDGE,"E6.1.0.3")])],"isStart":false}),makeQuery(id+"F8.opExtrude","CAP_FACE",FACE,{"disambiguationData":[OSD([sQuery(id+"F5.wireOp",EDGE,"E6.2.0.0"),sQuery(id+"F5.wireOp",EDGE,"E6.2.0.1"),sQuery(id+"F5.wireOp",EDGE,"E6.2.0.2"),sQuery(id+"F5.wireOp",EDGE,"E6.2.0.3")])],"isStart":false}),makeQuery(id+"F8.opExtrude","CAP_FACE",FACE,{"disambiguationData":[OSD([sQuery(id+"F5.wireOp",EDGE,"E6.3.0.0"),sQuery(id+"F5.wireOp",EDGE,"E6.3.0.1"),sQuery(id+"F5.wireOp",EDGE,"E6.3.0.2"),sQuery(id+"F5.wireOp",EDGE,"E6.3.0.3")])],"isStart":false}),makeQuery(id+"F8.opExtrude","CAP_FACE",FACE,{"disambiguationData":[OSD([sQuery(id+"F5.wireOp",EDGE,"E6.4.0.0"),sQuery(id+"F5.wireOp",EDGE,"E6.4.0.1"),sQuery(id+"F5.wireOp",EDGE,"E6.4.0.2"),sQuery(id+"F5.wireOp",EDGE,"E6.4.0.3")])],"isStart":false}),makeQuery(id+"F8.opExtrude","CAP_FACE",FACE,{"disambiguationData":[OSD([sQuery(id+"F5.wireOp",EDGE,"E6.5.0.0"),sQuery(id+"F5.wireOp",EDGE,"E6.5.0.1"),sQuery(id+"F5.wireOp",EDGE,"E6.5.0.2"),sQuery(id+"F5.wireOp",EDGE,"E6.5.0.3")])],"isStart":false}),makeQuery(id+"F8.opExtrude","CAP_FACE",FACE,{"disambiguationData":[OSD([sQuery(id+"F5.wireOp",EDGE,"E6.6.0.0"),sQuery(id+"F5.wireOp",EDGE,"E6.6.0.1"),sQuery(id+"F5.wireOp",EDGE,"E6.6.0.2"),sQuery(id+"F5.wireOp",EDGE,"E6.6.0.3")])],"isStart":false}),makeQuery(id+"F8.opExtrude","CAP_FACE",FACE,{"disambiguationData":[OSD([sQuery(id+"F5.wireOp",EDGE,"E6.7.0.0"),sQuery(id+"F5.wireOp",EDGE,"E6.7.0.1"),sQuery(id+"F5.wireOp",EDGE,"E6.7.0.2"),sQuery(id+"F5.wireOp",EDGE,"E6.7.0.3")])],"isStart":false}),makeQuery(id+"F8.opExtrude","CAP_FACE",FACE,{"disambiguationData":[OSD([sQuery(id+"F5.wireOp",EDGE,"E6.8.0.0"),sQuery(id+"F5.wireOp",EDGE,"E6.8.0.1"),sQuery(id+"F5.wireOp",EDGE,"E6.8.0.2"),sQuery(id+"F5.wireOp",EDGE,"E6.8.0.3")])],"isStart":false})]}),makeQuery(id+"F12.opExtrude","SWEPT_FACE",FACE,{"disambiguationData":[OSD([sQuery(id+"F11.wireOp",EDGE,"E16.MirrorC")])]})]});
            var Q5;
            Q5=makeQuery(id+"F12.boolean.opBoolean","INTERSECT",EDGE,{"derivedFrom":[makeQuery(id+"F8.boolean.opBoolean","MERGE",FACE,{"derivedFrom":[makeQuery(id+"F4.boolean.opBoolean","COPY",FACE,{"derivedFrom":makeQuery(id+"F4.opExtrude","CAP_FACE",FACE,{"disambiguationData":[OSD([sQuery(id+"F3.wireOp",EDGE,"E2.bottom"),sQuery(id+"F3.wireOp",EDGE,"E2.top"),sQuery(id+"F3.wireOp",EDGE,"E2.left"),sQuery(id+"F3.wireOp",EDGE,"E2.right")])],"isStart":false})}),makeQuery(id+"F4.boolean.opBoolean","COPY",FACE,{"derivedFrom":makeQuery(id+"F4.opExtrude","CAP_FACE",FACE,{"disambiguationData":[OSD([sQuery(id+"F3.wireOp",EDGE,"E3.bottom"),sQuery(id+"F3.wireOp",EDGE,"E3.top"),sQuery(id+"F3.wireOp",EDGE,"E3.left"),sQuery(id+"F3.wireOp",EDGE,"E3.right")])],"isStart":false})}),makeQuery(id+"F8.opExtrude","CAP_FACE",FACE,{"disambiguationData":[OSD([sQuery(id+"F5.wireOp",EDGE,"E5.bottom"),sQuery(id+"F5.wireOp",EDGE,"E5.top"),sQuery(id+"F5.wireOp",EDGE,"E5.left"),sQuery(id+"F5.wireOp",EDGE,"E5.right")])],"isStart":false}),makeQuery(id+"F8.opExtrude","CAP_FACE",FACE,{"disambiguationData":[OSD([sQuery(id+"F5.wireOp",EDGE,"E6.1.0.0"),sQuery(id+"F5.wireOp",EDGE,"E6.1.0.1"),sQuery(id+"F5.wireOp",EDGE,"E6.1.0.2"),sQuery(id+"F5.wireOp",EDGE,"E6.1.0.3")])],"isStart":false}),makeQuery(id+"F8.opExtrude","CAP_FACE",FACE,{"disambiguationData":[OSD([sQuery(id+"F5.wireOp",EDGE,"E6.2.0.0"),sQuery(id+"F5.wireOp",EDGE,"E6.2.0.1"),sQuery(id+"F5.wireOp",EDGE,"E6.2.0.2"),sQuery(id+"F5.wireOp",EDGE,"E6.2.0.3")])],"isStart":false}),makeQuery(id+"F8.opExtrude","CAP_FACE",FACE,{"disambiguationData":[OSD([sQuery(id+"F5.wireOp",EDGE,"E6.3.0.0"),sQuery(id+"F5.wireOp",EDGE,"E6.3.0.1"),sQuery(id+"F5.wireOp",EDGE,"E6.3.0.2"),sQuery(id+"F5.wireOp",EDGE,"E6.3.0.3")])],"isStart":false}),makeQuery(id+"F8.opExtrude","CAP_FACE",FACE,{"disambiguationData":[OSD([sQuery(id+"F5.wireOp",EDGE,"E6.4.0.0"),sQuery(id+"F5.wireOp",EDGE,"E6.4.0.1"),sQuery(id+"F5.wireOp",EDGE,"E6.4.0.2"),sQuery(id+"F5.wireOp",EDGE,"E6.4.0.3")])],"isStart":false}),makeQuery(id+"F8.opExtrude","CAP_FACE",FACE,{"disambiguationData":[OSD([sQuery(id+"F5.wireOp",EDGE,"E6.5.0.0"),sQuery(id+"F5.wireOp",EDGE,"E6.5.0.1"),sQuery(id+"F5.wireOp",EDGE,"E6.5.0.2"),sQuery(id+"F5.wireOp",EDGE,"E6.5.0.3")])],"isStart":false}),makeQuery(id+"F8.opExtrude","CAP_FACE",FACE,{"disambiguationData":[OSD([sQuery(id+"F5.wireOp",EDGE,"E6.6.0.0"),sQuery(id+"F5.wireOp",EDGE,"E6.6.0.1"),sQuery(id+"F5.wireOp",EDGE,"E6.6.0.2"),sQuery(id+"F5.wireOp",EDGE,"E6.6.0.3")])],"isStart":false}),makeQuery(id+"F8.opExtrude","CAP_FACE",FACE,{"disambiguationData":[OSD([sQuery(id+"F5.wireOp",EDGE,"E6.7.0.0"),sQuery(id+"F5.wireOp",EDGE,"E6.7.0.1"),sQuery(id+"F5.wireOp",EDGE,"E6.7.0.2"),sQuery(id+"F5.wireOp",EDGE,"E6.7.0.3")])],"isStart":false}),makeQuery(id+"F8.opExtrude","CAP_FACE",FACE,{"disambiguationData":[OSD([sQuery(id+"F5.wireOp",EDGE,"E6.8.0.0"),sQuery(id+"F5.wireOp",EDGE,"E6.8.0.1"),sQuery(id+"F5.wireOp",EDGE,"E6.8.0.2"),sQuery(id+"F5.wireOp",EDGE,"E6.8.0.3")])],"isStart":false})]}),makeQuery(id+"F12.opExtrude","SWEPT_FACE",FACE,{"disambiguationData":[OSD([sQuery(id+"F11.wireOp",EDGE,"E17.MirrorC")])]})]});
            var Q6;
            Q6=makeQuery(id+"F12.boolean.opBoolean","INTERSECT",EDGE,{"derivedFrom":[makeQuery(id+"F8.boolean.opBoolean","MERGE",FACE,{"derivedFrom":[makeQuery(id+"F4.boolean.opBoolean","COPY",FACE,{"derivedFrom":makeQuery(id+"F4.opExtrude","CAP_FACE",FACE,{"disambiguationData":[OSD([sQuery(id+"F3.wireOp",EDGE,"E2.bottom"),sQuery(id+"F3.wireOp",EDGE,"E2.top"),sQuery(id+"F3.wireOp",EDGE,"E2.left"),sQuery(id+"F3.wireOp",EDGE,"E2.right")])],"isStart":false})}),makeQuery(id+"F4.boolean.opBoolean","COPY",FACE,{"derivedFrom":makeQuery(id+"F4.opExtrude","CAP_FACE",FACE,{"disambiguationData":[OSD([sQuery(id+"F3.wireOp",EDGE,"E3.bottom"),sQuery(id+"F3.wireOp",EDGE,"E3.top"),sQuery(id+"F3.wireOp",EDGE,"E3.left"),sQuery(id+"F3.wireOp",EDGE,"E3.right")])],"isStart":false})}),makeQuery(id+"F8.opExtrude","CAP_FACE",FACE,{"disambiguationData":[OSD([sQuery(id+"F5.wireOp",EDGE,"E5.bottom"),sQuery(id+"F5.wireOp",EDGE,"E5.top"),sQuery(id+"F5.wireOp",EDGE,"E5.left"),sQuery(id+"F5.wireOp",EDGE,"E5.right")])],"isStart":false}),makeQuery(id+"F8.opExtrude","CAP_FACE",FACE,{"disambiguationData":[OSD([sQuery(id+"F5.wireOp",EDGE,"E6.1.0.0"),sQuery(id+"F5.wireOp",EDGE,"E6.1.0.1"),sQuery(id+"F5.wireOp",EDGE,"E6.1.0.2"),sQuery(id+"F5.wireOp",EDGE,"E6.1.0.3")])],"isStart":false}),makeQuery(id+"F8.opExtrude","CAP_FACE",FACE,{"disambiguationData":[OSD([sQuery(id+"F5.wireOp",EDGE,"E6.2.0.0"),sQuery(id+"F5.wireOp",EDGE,"E6.2.0.1"),sQuery(id+"F5.wireOp",EDGE,"E6.2.0.2"),sQuery(id+"F5.wireOp",EDGE,"E6.2.0.3")])],"isStart":false}),makeQuery(id+"F8.opExtrude","CAP_FACE",FACE,{"disambiguationData":[OSD([sQuery(id+"F5.wireOp",EDGE,"E6.3.0.0"),sQuery(id+"F5.wireOp",EDGE,"E6.3.0.1"),sQuery(id+"F5.wireOp",EDGE,"E6.3.0.2"),sQuery(id+"F5.wireOp",EDGE,"E6.3.0.3")])],"isStart":false}),makeQuery(id+"F8.opExtrude","CAP_FACE",FACE,{"disambiguationData":[OSD([sQuery(id+"F5.wireOp",EDGE,"E6.4.0.0"),sQuery(id+"F5.wireOp",EDGE,"E6.4.0.1"),sQuery(id+"F5.wireOp",EDGE,"E6.4.0.2"),sQuery(id+"F5.wireOp",EDGE,"E6.4.0.3")])],"isStart":false}),makeQuery(id+"F8.opExtrude","CAP_FACE",FACE,{"disambiguationData":[OSD([sQuery(id+"F5.wireOp",EDGE,"E6.5.0.0"),sQuery(id+"F5.wireOp",EDGE,"E6.5.0.1"),sQuery(id+"F5.wireOp",EDGE,"E6.5.0.2"),sQuery(id+"F5.wireOp",EDGE,"E6.5.0.3")])],"isStart":false}),makeQuery(id+"F8.opExtrude","CAP_FACE",FACE,{"disambiguationData":[OSD([sQuery(id+"F5.wireOp",EDGE,"E6.6.0.0"),sQuery(id+"F5.wireOp",EDGE,"E6.6.0.1"),sQuery(id+"F5.wireOp",EDGE,"E6.6.0.2"),sQuery(id+"F5.wireOp",EDGE,"E6.6.0.3")])],"isStart":false}),makeQuery(id+"F8.opExtrude","CAP_FACE",FACE,{"disambiguationData":[OSD([sQuery(id+"F5.wireOp",EDGE,"E6.7.0.0"),sQuery(id+"F5.wireOp",EDGE,"E6.7.0.1"),sQuery(id+"F5.wireOp",EDGE,"E6.7.0.2"),sQuery(id+"F5.wireOp",EDGE,"E6.7.0.3")])],"isStart":false}),makeQuery(id+"F8.opExtrude","CAP_FACE",FACE,{"disambiguationData":[OSD([sQuery(id+"F5.wireOp",EDGE,"E6.8.0.0"),sQuery(id+"F5.wireOp",EDGE,"E6.8.0.1"),sQuery(id+"F5.wireOp",EDGE,"E6.8.0.2"),sQuery(id+"F5.wireOp",EDGE,"E6.8.0.3")])],"isStart":false})]}),makeQuery(id+"F12.opExtrude","SWEPT_FACE",FACE,{"disambiguationData":[OSD([sQuery(id+"F11.wireOp",EDGE,"E18.MirrorC")])]})]});
            var Q7;
            Q7=makeQuery(id+"F12.boolean.opBoolean","INTERSECT",EDGE,{"derivedFrom":[makeQuery(id+"F8.boolean.opBoolean","MERGE",FACE,{"derivedFrom":[makeQuery(id+"F4.boolean.opBoolean","COPY",FACE,{"derivedFrom":makeQuery(id+"F4.opExtrude","CAP_FACE",FACE,{"disambiguationData":[OSD([sQuery(id+"F3.wireOp",EDGE,"E2.bottom"),sQuery(id+"F3.wireOp",EDGE,"E2.top"),sQuery(id+"F3.wireOp",EDGE,"E2.left"),sQuery(id+"F3.wireOp",EDGE,"E2.right")])],"isStart":false})}),makeQuery(id+"F4.boolean.opBoolean","COPY",FACE,{"derivedFrom":makeQuery(id+"F4.opExtrude","CAP_FACE",FACE,{"disambiguationData":[OSD([sQuery(id+"F3.wireOp",EDGE,"E3.bottom"),sQuery(id+"F3.wireOp",EDGE,"E3.top"),sQuery(id+"F3.wireOp",EDGE,"E3.left"),sQuery(id+"F3.wireOp",EDGE,"E3.right")])],"isStart":false})}),makeQuery(id+"F8.opExtrude","CAP_FACE",FACE,{"disambiguationData":[OSD([sQuery(id+"F5.wireOp",EDGE,"E5.bottom"),sQuery(id+"F5.wireOp",EDGE,"E5.top"),sQuery(id+"F5.wireOp",EDGE,"E5.left"),sQuery(id+"F5.wireOp",EDGE,"E5.right")])],"isStart":false}),makeQuery(id+"F8.opExtrude","CAP_FACE",FACE,{"disambiguationData":[OSD([sQuery(id+"F5.wireOp",EDGE,"E6.1.0.0"),sQuery(id+"F5.wireOp",EDGE,"E6.1.0.1"),sQuery(id+"F5.wireOp",EDGE,"E6.1.0.2"),sQuery(id+"F5.wireOp",EDGE,"E6.1.0.3")])],"isStart":false}),makeQuery(id+"F8.opExtrude","CAP_FACE",FACE,{"disambiguationData":[OSD([sQuery(id+"F5.wireOp",EDGE,"E6.2.0.0"),sQuery(id+"F5.wireOp",EDGE,"E6.2.0.1"),sQuery(id+"F5.wireOp",EDGE,"E6.2.0.2"),sQuery(id+"F5.wireOp",EDGE,"E6.2.0.3")])],"isStart":false}),makeQuery(id+"F8.opExtrude","CAP_FACE",FACE,{"disambiguationData":[OSD([sQuery(id+"F5.wireOp",EDGE,"E6.3.0.0"),sQuery(id+"F5.wireOp",EDGE,"E6.3.0.1"),sQuery(id+"F5.wireOp",EDGE,"E6.3.0.2"),sQuery(id+"F5.wireOp",EDGE,"E6.3.0.3")])],"isStart":false}),makeQuery(id+"F8.opExtrude","CAP_FACE",FACE,{"disambiguationData":[OSD([sQuery(id+"F5.wireOp",EDGE,"E6.4.0.0"),sQuery(id+"F5.wireOp",EDGE,"E6.4.0.1"),sQuery(id+"F5.wireOp",EDGE,"E6.4.0.2"),sQuery(id+"F5.wireOp",EDGE,"E6.4.0.3")])],"isStart":false}),makeQuery(id+"F8.opExtrude","CAP_FACE",FACE,{"disambiguationData":[OSD([sQuery(id+"F5.wireOp",EDGE,"E6.5.0.0"),sQuery(id+"F5.wireOp",EDGE,"E6.5.0.1"),sQuery(id+"F5.wireOp",EDGE,"E6.5.0.2"),sQuery(id+"F5.wireOp",EDGE,"E6.5.0.3")])],"isStart":false}),makeQuery(id+"F8.opExtrude","CAP_FACE",FACE,{"disambiguationData":[OSD([sQuery(id+"F5.wireOp",EDGE,"E6.6.0.0"),sQuery(id+"F5.wireOp",EDGE,"E6.6.0.1"),sQuery(id+"F5.wireOp",EDGE,"E6.6.0.2"),sQuery(id+"F5.wireOp",EDGE,"E6.6.0.3")])],"isStart":false}),makeQuery(id+"F8.opExtrude","CAP_FACE",FACE,{"disambiguationData":[OSD([sQuery(id+"F5.wireOp",EDGE,"E6.7.0.0"),sQuery(id+"F5.wireOp",EDGE,"E6.7.0.1"),sQuery(id+"F5.wireOp",EDGE,"E6.7.0.2"),sQuery(id+"F5.wireOp",EDGE,"E6.7.0.3")])],"isStart":false}),makeQuery(id+"F8.opExtrude","CAP_FACE",FACE,{"disambiguationData":[OSD([sQuery(id+"F5.wireOp",EDGE,"E6.8.0.0"),sQuery(id+"F5.wireOp",EDGE,"E6.8.0.1"),sQuery(id+"F5.wireOp",EDGE,"E6.8.0.2"),sQuery(id+"F5.wireOp",EDGE,"E6.8.0.3")])],"isStart":false})]}),makeQuery(id+"F12.opExtrude","SWEPT_FACE",FACE,{"disambiguationData":[OSD([sQuery(id+"F11.wireOp",EDGE,"E19.MirrorC")])]})]});
            var Q8;
            Q8=makeQuery(id+"F12.boolean.opBoolean","INTERSECT",EDGE,{"derivedFrom":[makeQuery(id+"F8.boolean.opBoolean","MERGE",FACE,{"derivedFrom":[makeQuery(id+"F4.boolean.opBoolean","COPY",FACE,{"derivedFrom":makeQuery(id+"F4.opExtrude","CAP_FACE",FACE,{"disambiguationData":[OSD([sQuery(id+"F3.wireOp",EDGE,"E2.bottom"),sQuery(id+"F3.wireOp",EDGE,"E2.top"),sQuery(id+"F3.wireOp",EDGE,"E2.left"),sQuery(id+"F3.wireOp",EDGE,"E2.right")])],"isStart":false})}),makeQuery(id+"F4.boolean.opBoolean","COPY",FACE,{"derivedFrom":makeQuery(id+"F4.opExtrude","CAP_FACE",FACE,{"disambiguationData":[OSD([sQuery(id+"F3.wireOp",EDGE,"E3.bottom"),sQuery(id+"F3.wireOp",EDGE,"E3.top"),sQuery(id+"F3.wireOp",EDGE,"E3.left"),sQuery(id+"F3.wireOp",EDGE,"E3.right")])],"isStart":false})}),makeQuery(id+"F8.opExtrude","CAP_FACE",FACE,{"disambiguationData":[OSD([sQuery(id+"F5.wireOp",EDGE,"E5.bottom"),sQuery(id+"F5.wireOp",EDGE,"E5.top"),sQuery(id+"F5.wireOp",EDGE,"E5.left"),sQuery(id+"F5.wireOp",EDGE,"E5.right")])],"isStart":false}),makeQuery(id+"F8.opExtrude","CAP_FACE",FACE,{"disambiguationData":[OSD([sQuery(id+"F5.wireOp",EDGE,"E6.1.0.0"),sQuery(id+"F5.wireOp",EDGE,"E6.1.0.1"),sQuery(id+"F5.wireOp",EDGE,"E6.1.0.2"),sQuery(id+"F5.wireOp",EDGE,"E6.1.0.3")])],"isStart":false}),makeQuery(id+"F8.opExtrude","CAP_FACE",FACE,{"disambiguationData":[OSD([sQuery(id+"F5.wireOp",EDGE,"E6.2.0.0"),sQuery(id+"F5.wireOp",EDGE,"E6.2.0.1"),sQuery(id+"F5.wireOp",EDGE,"E6.2.0.2"),sQuery(id+"F5.wireOp",EDGE,"E6.2.0.3")])],"isStart":false}),makeQuery(id+"F8.opExtrude","CAP_FACE",FACE,{"disambiguationData":[OSD([sQuery(id+"F5.wireOp",EDGE,"E6.3.0.0"),sQuery(id+"F5.wireOp",EDGE,"E6.3.0.1"),sQuery(id+"F5.wireOp",EDGE,"E6.3.0.2"),sQuery(id+"F5.wireOp",EDGE,"E6.3.0.3")])],"isStart":false}),makeQuery(id+"F8.opExtrude","CAP_FACE",FACE,{"disambiguationData":[OSD([sQuery(id+"F5.wireOp",EDGE,"E6.4.0.0"),sQuery(id+"F5.wireOp",EDGE,"E6.4.0.1"),sQuery(id+"F5.wireOp",EDGE,"E6.4.0.2"),sQuery(id+"F5.wireOp",EDGE,"E6.4.0.3")])],"isStart":false}),makeQuery(id+"F8.opExtrude","CAP_FACE",FACE,{"disambiguationData":[OSD([sQuery(id+"F5.wireOp",EDGE,"E6.5.0.0"),sQuery(id+"F5.wireOp",EDGE,"E6.5.0.1"),sQuery(id+"F5.wireOp",EDGE,"E6.5.0.2"),sQuery(id+"F5.wireOp",EDGE,"E6.5.0.3")])],"isStart":false}),makeQuery(id+"F8.opExtrude","CAP_FACE",FACE,{"disambiguationData":[OSD([sQuery(id+"F5.wireOp",EDGE,"E6.6.0.0"),sQuery(id+"F5.wireOp",EDGE,"E6.6.0.1"),sQuery(id+"F5.wireOp",EDGE,"E6.6.0.2"),sQuery(id+"F5.wireOp",EDGE,"E6.6.0.3")])],"isStart":false}),makeQuery(id+"F8.opExtrude","CAP_FACE",FACE,{"disambiguationData":[OSD([sQuery(id+"F5.wireOp",EDGE,"E6.7.0.0"),sQuery(id+"F5.wireOp",EDGE,"E6.7.0.1"),sQuery(id+"F5.wireOp",EDGE,"E6.7.0.2"),sQuery(id+"F5.wireOp",EDGE,"E6.7.0.3")])],"isStart":false}),makeQuery(id+"F8.opExtrude","CAP_FACE",FACE,{"disambiguationData":[OSD([sQuery(id+"F5.wireOp",EDGE,"E6.8.0.0"),sQuery(id+"F5.wireOp",EDGE,"E6.8.0.1"),sQuery(id+"F5.wireOp",EDGE,"E6.8.0.2"),sQuery(id+"F5.wireOp",EDGE,"E6.8.0.3")])],"isStart":false})]}),makeQuery(id+"F12.opExtrude","SWEPT_FACE",FACE,{"disambiguationData":[OSD([sQuery(id+"F11.wireOp",EDGE,"E20.MirrorC")])]})]});
            var Q9;
            Q9=makeQuery(id+"F12.boolean.opBoolean","INTERSECT",EDGE,{"derivedFrom":[makeQuery(id+"F8.boolean.opBoolean","MERGE",FACE,{"derivedFrom":[makeQuery(id+"F4.boolean.opBoolean","COPY",FACE,{"derivedFrom":makeQuery(id+"F4.opExtrude","CAP_FACE",FACE,{"disambiguationData":[OSD([sQuery(id+"F3.wireOp",EDGE,"E2.bottom"),sQuery(id+"F3.wireOp",EDGE,"E2.top"),sQuery(id+"F3.wireOp",EDGE,"E2.left"),sQuery(id+"F3.wireOp",EDGE,"E2.right")])],"isStart":false})}),makeQuery(id+"F4.boolean.opBoolean","COPY",FACE,{"derivedFrom":makeQuery(id+"F4.opExtrude","CAP_FACE",FACE,{"disambiguationData":[OSD([sQuery(id+"F3.wireOp",EDGE,"E3.bottom"),sQuery(id+"F3.wireOp",EDGE,"E3.top"),sQuery(id+"F3.wireOp",EDGE,"E3.left"),sQuery(id+"F3.wireOp",EDGE,"E3.right")])],"isStart":false})}),makeQuery(id+"F8.opExtrude","CAP_FACE",FACE,{"disambiguationData":[OSD([sQuery(id+"F5.wireOp",EDGE,"E5.bottom"),sQuery(id+"F5.wireOp",EDGE,"E5.top"),sQuery(id+"F5.wireOp",EDGE,"E5.left"),sQuery(id+"F5.wireOp",EDGE,"E5.right")])],"isStart":false}),makeQuery(id+"F8.opExtrude","CAP_FACE",FACE,{"disambiguationData":[OSD([sQuery(id+"F5.wireOp",EDGE,"E6.1.0.0"),sQuery(id+"F5.wireOp",EDGE,"E6.1.0.1"),sQuery(id+"F5.wireOp",EDGE,"E6.1.0.2"),sQuery(id+"F5.wireOp",EDGE,"E6.1.0.3")])],"isStart":false}),makeQuery(id+"F8.opExtrude","CAP_FACE",FACE,{"disambiguationData":[OSD([sQuery(id+"F5.wireOp",EDGE,"E6.2.0.0"),sQuery(id+"F5.wireOp",EDGE,"E6.2.0.1"),sQuery(id+"F5.wireOp",EDGE,"E6.2.0.2"),sQuery(id+"F5.wireOp",EDGE,"E6.2.0.3")])],"isStart":false}),makeQuery(id+"F8.opExtrude","CAP_FACE",FACE,{"disambiguationData":[OSD([sQuery(id+"F5.wireOp",EDGE,"E6.3.0.0"),sQuery(id+"F5.wireOp",EDGE,"E6.3.0.1"),sQuery(id+"F5.wireOp",EDGE,"E6.3.0.2"),sQuery(id+"F5.wireOp",EDGE,"E6.3.0.3")])],"isStart":false}),makeQuery(id+"F8.opExtrude","CAP_FACE",FACE,{"disambiguationData":[OSD([sQuery(id+"F5.wireOp",EDGE,"E6.4.0.0"),sQuery(id+"F5.wireOp",EDGE,"E6.4.0.1"),sQuery(id+"F5.wireOp",EDGE,"E6.4.0.2"),sQuery(id+"F5.wireOp",EDGE,"E6.4.0.3")])],"isStart":false}),makeQuery(id+"F8.opExtrude","CAP_FACE",FACE,{"disambiguationData":[OSD([sQuery(id+"F5.wireOp",EDGE,"E6.5.0.0"),sQuery(id+"F5.wireOp",EDGE,"E6.5.0.1"),sQuery(id+"F5.wireOp",EDGE,"E6.5.0.2"),sQuery(id+"F5.wireOp",EDGE,"E6.5.0.3")])],"isStart":false}),makeQuery(id+"F8.opExtrude","CAP_FACE",FACE,{"disambiguationData":[OSD([sQuery(id+"F5.wireOp",EDGE,"E6.6.0.0"),sQuery(id+"F5.wireOp",EDGE,"E6.6.0.1"),sQuery(id+"F5.wireOp",EDGE,"E6.6.0.2"),sQuery(id+"F5.wireOp",EDGE,"E6.6.0.3")])],"isStart":false}),makeQuery(id+"F8.opExtrude","CAP_FACE",FACE,{"disambiguationData":[OSD([sQuery(id+"F5.wireOp",EDGE,"E6.7.0.0"),sQuery(id+"F5.wireOp",EDGE,"E6.7.0.1"),sQuery(id+"F5.wireOp",EDGE,"E6.7.0.2"),sQuery(id+"F5.wireOp",EDGE,"E6.7.0.3")])],"isStart":false}),makeQuery(id+"F8.opExtrude","CAP_FACE",FACE,{"disambiguationData":[OSD([sQuery(id+"F5.wireOp",EDGE,"E6.8.0.0"),sQuery(id+"F5.wireOp",EDGE,"E6.8.0.1"),sQuery(id+"F5.wireOp",EDGE,"E6.8.0.2"),sQuery(id+"F5.wireOp",EDGE,"E6.8.0.3")])],"isStart":false})]}),makeQuery(id+"F12.opExtrude","SWEPT_FACE",FACE,{"disambiguationData":[OSD([sQuery(id+"F11.wireOp",EDGE,"E8")])]})]});
            var Q10;
            Q10=makeQuery(id+"F12.boolean.opBoolean","INTERSECT",EDGE,{"derivedFrom":[makeQuery(id+"F8.boolean.opBoolean","MERGE",FACE,{"derivedFrom":[makeQuery(id+"F4.boolean.opBoolean","COPY",FACE,{"derivedFrom":makeQuery(id+"F4.opExtrude","CAP_FACE",FACE,{"disambiguationData":[OSD([sQuery(id+"F3.wireOp",EDGE,"E2.bottom"),sQuery(id+"F3.wireOp",EDGE,"E2.top"),sQuery(id+"F3.wireOp",EDGE,"E2.left"),sQuery(id+"F3.wireOp",EDGE,"E2.right")])],"isStart":false})}),makeQuery(id+"F4.boolean.opBoolean","COPY",FACE,{"derivedFrom":makeQuery(id+"F4.opExtrude","CAP_FACE",FACE,{"disambiguationData":[OSD([sQuery(id+"F3.wireOp",EDGE,"E3.bottom"),sQuery(id+"F3.wireOp",EDGE,"E3.top"),sQuery(id+"F3.wireOp",EDGE,"E3.left"),sQuery(id+"F3.wireOp",EDGE,"E3.right")])],"isStart":false})}),makeQuery(id+"F8.opExtrude","CAP_FACE",FACE,{"disambiguationData":[OSD([sQuery(id+"F5.wireOp",EDGE,"E5.bottom"),sQuery(id+"F5.wireOp",EDGE,"E5.top"),sQuery(id+"F5.wireOp",EDGE,"E5.left"),sQuery(id+"F5.wireOp",EDGE,"E5.right")])],"isStart":false}),makeQuery(id+"F8.opExtrude","CAP_FACE",FACE,{"disambiguationData":[OSD([sQuery(id+"F5.wireOp",EDGE,"E6.1.0.0"),sQuery(id+"F5.wireOp",EDGE,"E6.1.0.1"),sQuery(id+"F5.wireOp",EDGE,"E6.1.0.2"),sQuery(id+"F5.wireOp",EDGE,"E6.1.0.3")])],"isStart":false}),makeQuery(id+"F8.opExtrude","CAP_FACE",FACE,{"disambiguationData":[OSD([sQuery(id+"F5.wireOp",EDGE,"E6.2.0.0"),sQuery(id+"F5.wireOp",EDGE,"E6.2.0.1"),sQuery(id+"F5.wireOp",EDGE,"E6.2.0.2"),sQuery(id+"F5.wireOp",EDGE,"E6.2.0.3")])],"isStart":false}),makeQuery(id+"F8.opExtrude","CAP_FACE",FACE,{"disambiguationData":[OSD([sQuery(id+"F5.wireOp",EDGE,"E6.3.0.0"),sQuery(id+"F5.wireOp",EDGE,"E6.3.0.1"),sQuery(id+"F5.wireOp",EDGE,"E6.3.0.2"),sQuery(id+"F5.wireOp",EDGE,"E6.3.0.3")])],"isStart":false}),makeQuery(id+"F8.opExtrude","CAP_FACE",FACE,{"disambiguationData":[OSD([sQuery(id+"F5.wireOp",EDGE,"E6.4.0.0"),sQuery(id+"F5.wireOp",EDGE,"E6.4.0.1"),sQuery(id+"F5.wireOp",EDGE,"E6.4.0.2"),sQuery(id+"F5.wireOp",EDGE,"E6.4.0.3")])],"isStart":false}),makeQuery(id+"F8.opExtrude","CAP_FACE",FACE,{"disambiguationData":[OSD([sQuery(id+"F5.wireOp",EDGE,"E6.5.0.0"),sQuery(id+"F5.wireOp",EDGE,"E6.5.0.1"),sQuery(id+"F5.wireOp",EDGE,"E6.5.0.2"),sQuery(id+"F5.wireOp",EDGE,"E6.5.0.3")])],"isStart":false}),makeQuery(id+"F8.opExtrude","CAP_FACE",FACE,{"disambiguationData":[OSD([sQuery(id+"F5.wireOp",EDGE,"E6.6.0.0"),sQuery(id+"F5.wireOp",EDGE,"E6.6.0.1"),sQuery(id+"F5.wireOp",EDGE,"E6.6.0.2"),sQuery(id+"F5.wireOp",EDGE,"E6.6.0.3")])],"isStart":false}),makeQuery(id+"F8.opExtrude","CAP_FACE",FACE,{"disambiguationData":[OSD([sQuery(id+"F5.wireOp",EDGE,"E6.7.0.0"),sQuery(id+"F5.wireOp",EDGE,"E6.7.0.1"),sQuery(id+"F5.wireOp",EDGE,"E6.7.0.2"),sQuery(id+"F5.wireOp",EDGE,"E6.7.0.3")])],"isStart":false}),makeQuery(id+"F8.opExtrude","CAP_FACE",FACE,{"disambiguationData":[OSD([sQuery(id+"F5.wireOp",EDGE,"E6.8.0.0"),sQuery(id+"F5.wireOp",EDGE,"E6.8.0.1"),sQuery(id+"F5.wireOp",EDGE,"E6.8.0.2"),sQuery(id+"F5.wireOp",EDGE,"E6.8.0.3")])],"isStart":false})]}),makeQuery(id+"F12.opExtrude","SWEPT_FACE",FACE,{"disambiguationData":[OSD([sQuery(id+"F11.wireOp",EDGE,"E10.1.0.0")])]})]});
            var Q11;
            Q11=makeQuery(id+"F12.boolean.opBoolean","INTERSECT",EDGE,{"derivedFrom":[makeQuery(id+"F8.boolean.opBoolean","MERGE",FACE,{"derivedFrom":[makeQuery(id+"F4.boolean.opBoolean","COPY",FACE,{"derivedFrom":makeQuery(id+"F4.opExtrude","CAP_FACE",FACE,{"disambiguationData":[OSD([sQuery(id+"F3.wireOp",EDGE,"E2.bottom"),sQuery(id+"F3.wireOp",EDGE,"E2.top"),sQuery(id+"F3.wireOp",EDGE,"E2.left"),sQuery(id+"F3.wireOp",EDGE,"E2.right")])],"isStart":false})}),makeQuery(id+"F4.boolean.opBoolean","COPY",FACE,{"derivedFrom":makeQuery(id+"F4.opExtrude","CAP_FACE",FACE,{"disambiguationData":[OSD([sQuery(id+"F3.wireOp",EDGE,"E3.bottom"),sQuery(id+"F3.wireOp",EDGE,"E3.top"),sQuery(id+"F3.wireOp",EDGE,"E3.left"),sQuery(id+"F3.wireOp",EDGE,"E3.right")])],"isStart":false})}),makeQuery(id+"F8.opExtrude","CAP_FACE",FACE,{"disambiguationData":[OSD([sQuery(id+"F5.wireOp",EDGE,"E5.bottom"),sQuery(id+"F5.wireOp",EDGE,"E5.top"),sQuery(id+"F5.wireOp",EDGE,"E5.left"),sQuery(id+"F5.wireOp",EDGE,"E5.right")])],"isStart":false}),makeQuery(id+"F8.opExtrude","CAP_FACE",FACE,{"disambiguationData":[OSD([sQuery(id+"F5.wireOp",EDGE,"E6.1.0.0"),sQuery(id+"F5.wireOp",EDGE,"E6.1.0.1"),sQuery(id+"F5.wireOp",EDGE,"E6.1.0.2"),sQuery(id+"F5.wireOp",EDGE,"E6.1.0.3")])],"isStart":false}),makeQuery(id+"F8.opExtrude","CAP_FACE",FACE,{"disambiguationData":[OSD([sQuery(id+"F5.wireOp",EDGE,"E6.2.0.0"),sQuery(id+"F5.wireOp",EDGE,"E6.2.0.1"),sQuery(id+"F5.wireOp",EDGE,"E6.2.0.2"),sQuery(id+"F5.wireOp",EDGE,"E6.2.0.3")])],"isStart":false}),makeQuery(id+"F8.opExtrude","CAP_FACE",FACE,{"disambiguationData":[OSD([sQuery(id+"F5.wireOp",EDGE,"E6.3.0.0"),sQuery(id+"F5.wireOp",EDGE,"E6.3.0.1"),sQuery(id+"F5.wireOp",EDGE,"E6.3.0.2"),sQuery(id+"F5.wireOp",EDGE,"E6.3.0.3")])],"isStart":false}),makeQuery(id+"F8.opExtrude","CAP_FACE",FACE,{"disambiguationData":[OSD([sQuery(id+"F5.wireOp",EDGE,"E6.4.0.0"),sQuery(id+"F5.wireOp",EDGE,"E6.4.0.1"),sQuery(id+"F5.wireOp",EDGE,"E6.4.0.2"),sQuery(id+"F5.wireOp",EDGE,"E6.4.0.3")])],"isStart":false}),makeQuery(id+"F8.opExtrude","CAP_FACE",FACE,{"disambiguationData":[OSD([sQuery(id+"F5.wireOp",EDGE,"E6.5.0.0"),sQuery(id+"F5.wireOp",EDGE,"E6.5.0.1"),sQuery(id+"F5.wireOp",EDGE,"E6.5.0.2"),sQuery(id+"F5.wireOp",EDGE,"E6.5.0.3")])],"isStart":false}),makeQuery(id+"F8.opExtrude","CAP_FACE",FACE,{"disambiguationData":[OSD([sQuery(id+"F5.wireOp",EDGE,"E6.6.0.0"),sQuery(id+"F5.wireOp",EDGE,"E6.6.0.1"),sQuery(id+"F5.wireOp",EDGE,"E6.6.0.2"),sQuery(id+"F5.wireOp",EDGE,"E6.6.0.3")])],"isStart":false}),makeQuery(id+"F8.opExtrude","CAP_FACE",FACE,{"disambiguationData":[OSD([sQuery(id+"F5.wireOp",EDGE,"E6.7.0.0"),sQuery(id+"F5.wireOp",EDGE,"E6.7.0.1"),sQuery(id+"F5.wireOp",EDGE,"E6.7.0.2"),sQuery(id+"F5.wireOp",EDGE,"E6.7.0.3")])],"isStart":false}),makeQuery(id+"F8.opExtrude","CAP_FACE",FACE,{"disambiguationData":[OSD([sQuery(id+"F5.wireOp",EDGE,"E6.8.0.0"),sQuery(id+"F5.wireOp",EDGE,"E6.8.0.1"),sQuery(id+"F5.wireOp",EDGE,"E6.8.0.2"),sQuery(id+"F5.wireOp",EDGE,"E6.8.0.3")])],"isStart":false})]}),makeQuery(id+"F12.opExtrude","SWEPT_FACE",FACE,{"disambiguationData":[OSD([sQuery(id+"F11.wireOp",EDGE,"E10.2.0.0")])]})]});
            var Q12;
            Q12=makeQuery(id+"F12.boolean.opBoolean","INTERSECT",EDGE,{"derivedFrom":[makeQuery(id+"F8.boolean.opBoolean","MERGE",FACE,{"derivedFrom":[makeQuery(id+"F4.boolean.opBoolean","COPY",FACE,{"derivedFrom":makeQuery(id+"F4.opExtrude","CAP_FACE",FACE,{"disambiguationData":[OSD([sQuery(id+"F3.wireOp",EDGE,"E2.bottom"),sQuery(id+"F3.wireOp",EDGE,"E2.top"),sQuery(id+"F3.wireOp",EDGE,"E2.left"),sQuery(id+"F3.wireOp",EDGE,"E2.right")])],"isStart":false})}),makeQuery(id+"F4.boolean.opBoolean","COPY",FACE,{"derivedFrom":makeQuery(id+"F4.opExtrude","CAP_FACE",FACE,{"disambiguationData":[OSD([sQuery(id+"F3.wireOp",EDGE,"E3.bottom"),sQuery(id+"F3.wireOp",EDGE,"E3.top"),sQuery(id+"F3.wireOp",EDGE,"E3.left"),sQuery(id+"F3.wireOp",EDGE,"E3.right")])],"isStart":false})}),makeQuery(id+"F8.opExtrude","CAP_FACE",FACE,{"disambiguationData":[OSD([sQuery(id+"F5.wireOp",EDGE,"E5.bottom"),sQuery(id+"F5.wireOp",EDGE,"E5.top"),sQuery(id+"F5.wireOp",EDGE,"E5.left"),sQuery(id+"F5.wireOp",EDGE,"E5.right")])],"isStart":false}),makeQuery(id+"F8.opExtrude","CAP_FACE",FACE,{"disambiguationData":[OSD([sQuery(id+"F5.wireOp",EDGE,"E6.1.0.0"),sQuery(id+"F5.wireOp",EDGE,"E6.1.0.1"),sQuery(id+"F5.wireOp",EDGE,"E6.1.0.2"),sQuery(id+"F5.wireOp",EDGE,"E6.1.0.3")])],"isStart":false}),makeQuery(id+"F8.opExtrude","CAP_FACE",FACE,{"disambiguationData":[OSD([sQuery(id+"F5.wireOp",EDGE,"E6.2.0.0"),sQuery(id+"F5.wireOp",EDGE,"E6.2.0.1"),sQuery(id+"F5.wireOp",EDGE,"E6.2.0.2"),sQuery(id+"F5.wireOp",EDGE,"E6.2.0.3")])],"isStart":false}),makeQuery(id+"F8.opExtrude","CAP_FACE",FACE,{"disambiguationData":[OSD([sQuery(id+"F5.wireOp",EDGE,"E6.3.0.0"),sQuery(id+"F5.wireOp",EDGE,"E6.3.0.1"),sQuery(id+"F5.wireOp",EDGE,"E6.3.0.2"),sQuery(id+"F5.wireOp",EDGE,"E6.3.0.3")])],"isStart":false}),makeQuery(id+"F8.opExtrude","CAP_FACE",FACE,{"disambiguationData":[OSD([sQuery(id+"F5.wireOp",EDGE,"E6.4.0.0"),sQuery(id+"F5.wireOp",EDGE,"E6.4.0.1"),sQuery(id+"F5.wireOp",EDGE,"E6.4.0.2"),sQuery(id+"F5.wireOp",EDGE,"E6.4.0.3")])],"isStart":false}),makeQuery(id+"F8.opExtrude","CAP_FACE",FACE,{"disambiguationData":[OSD([sQuery(id+"F5.wireOp",EDGE,"E6.5.0.0"),sQuery(id+"F5.wireOp",EDGE,"E6.5.0.1"),sQuery(id+"F5.wireOp",EDGE,"E6.5.0.2"),sQuery(id+"F5.wireOp",EDGE,"E6.5.0.3")])],"isStart":false}),makeQuery(id+"F8.opExtrude","CAP_FACE",FACE,{"disambiguationData":[OSD([sQuery(id+"F5.wireOp",EDGE,"E6.6.0.0"),sQuery(id+"F5.wireOp",EDGE,"E6.6.0.1"),sQuery(id+"F5.wireOp",EDGE,"E6.6.0.2"),sQuery(id+"F5.wireOp",EDGE,"E6.6.0.3")])],"isStart":false}),makeQuery(id+"F8.opExtrude","CAP_FACE",FACE,{"disambiguationData":[OSD([sQuery(id+"F5.wireOp",EDGE,"E6.7.0.0"),sQuery(id+"F5.wireOp",EDGE,"E6.7.0.1"),sQuery(id+"F5.wireOp",EDGE,"E6.7.0.2"),sQuery(id+"F5.wireOp",EDGE,"E6.7.0.3")])],"isStart":false}),makeQuery(id+"F8.opExtrude","CAP_FACE",FACE,{"disambiguationData":[OSD([sQuery(id+"F5.wireOp",EDGE,"E6.8.0.0"),sQuery(id+"F5.wireOp",EDGE,"E6.8.0.1"),sQuery(id+"F5.wireOp",EDGE,"E6.8.0.2"),sQuery(id+"F5.wireOp",EDGE,"E6.8.0.3")])],"isStart":false})]}),makeQuery(id+"F12.opExtrude","SWEPT_FACE",FACE,{"disambiguationData":[OSD([sQuery(id+"F11.wireOp",EDGE,"E10.3.0.0")])]})]});
            var Q13;
            Q13=makeQuery(id+"F12.boolean.opBoolean","INTERSECT",EDGE,{"derivedFrom":[makeQuery(id+"F8.boolean.opBoolean","MERGE",FACE,{"derivedFrom":[makeQuery(id+"F4.boolean.opBoolean","COPY",FACE,{"derivedFrom":makeQuery(id+"F4.opExtrude","CAP_FACE",FACE,{"disambiguationData":[OSD([sQuery(id+"F3.wireOp",EDGE,"E2.bottom"),sQuery(id+"F3.wireOp",EDGE,"E2.top"),sQuery(id+"F3.wireOp",EDGE,"E2.left"),sQuery(id+"F3.wireOp",EDGE,"E2.right")])],"isStart":false})}),makeQuery(id+"F4.boolean.opBoolean","COPY",FACE,{"derivedFrom":makeQuery(id+"F4.opExtrude","CAP_FACE",FACE,{"disambiguationData":[OSD([sQuery(id+"F3.wireOp",EDGE,"E3.bottom"),sQuery(id+"F3.wireOp",EDGE,"E3.top"),sQuery(id+"F3.wireOp",EDGE,"E3.left"),sQuery(id+"F3.wireOp",EDGE,"E3.right")])],"isStart":false})}),makeQuery(id+"F8.opExtrude","CAP_FACE",FACE,{"disambiguationData":[OSD([sQuery(id+"F5.wireOp",EDGE,"E5.bottom"),sQuery(id+"F5.wireOp",EDGE,"E5.top"),sQuery(id+"F5.wireOp",EDGE,"E5.left"),sQuery(id+"F5.wireOp",EDGE,"E5.right")])],"isStart":false}),makeQuery(id+"F8.opExtrude","CAP_FACE",FACE,{"disambiguationData":[OSD([sQuery(id+"F5.wireOp",EDGE,"E6.1.0.0"),sQuery(id+"F5.wireOp",EDGE,"E6.1.0.1"),sQuery(id+"F5.wireOp",EDGE,"E6.1.0.2"),sQuery(id+"F5.wireOp",EDGE,"E6.1.0.3")])],"isStart":false}),makeQuery(id+"F8.opExtrude","CAP_FACE",FACE,{"disambiguationData":[OSD([sQuery(id+"F5.wireOp",EDGE,"E6.2.0.0"),sQuery(id+"F5.wireOp",EDGE,"E6.2.0.1"),sQuery(id+"F5.wireOp",EDGE,"E6.2.0.2"),sQuery(id+"F5.wireOp",EDGE,"E6.2.0.3")])],"isStart":false}),makeQuery(id+"F8.opExtrude","CAP_FACE",FACE,{"disambiguationData":[OSD([sQuery(id+"F5.wireOp",EDGE,"E6.3.0.0"),sQuery(id+"F5.wireOp",EDGE,"E6.3.0.1"),sQuery(id+"F5.wireOp",EDGE,"E6.3.0.2"),sQuery(id+"F5.wireOp",EDGE,"E6.3.0.3")])],"isStart":false}),makeQuery(id+"F8.opExtrude","CAP_FACE",FACE,{"disambiguationData":[OSD([sQuery(id+"F5.wireOp",EDGE,"E6.4.0.0"),sQuery(id+"F5.wireOp",EDGE,"E6.4.0.1"),sQuery(id+"F5.wireOp",EDGE,"E6.4.0.2"),sQuery(id+"F5.wireOp",EDGE,"E6.4.0.3")])],"isStart":false}),makeQuery(id+"F8.opExtrude","CAP_FACE",FACE,{"disambiguationData":[OSD([sQuery(id+"F5.wireOp",EDGE,"E6.5.0.0"),sQuery(id+"F5.wireOp",EDGE,"E6.5.0.1"),sQuery(id+"F5.wireOp",EDGE,"E6.5.0.2"),sQuery(id+"F5.wireOp",EDGE,"E6.5.0.3")])],"isStart":false}),makeQuery(id+"F8.opExtrude","CAP_FACE",FACE,{"disambiguationData":[OSD([sQuery(id+"F5.wireOp",EDGE,"E6.6.0.0"),sQuery(id+"F5.wireOp",EDGE,"E6.6.0.1"),sQuery(id+"F5.wireOp",EDGE,"E6.6.0.2"),sQuery(id+"F5.wireOp",EDGE,"E6.6.0.3")])],"isStart":false}),makeQuery(id+"F8.opExtrude","CAP_FACE",FACE,{"disambiguationData":[OSD([sQuery(id+"F5.wireOp",EDGE,"E6.7.0.0"),sQuery(id+"F5.wireOp",EDGE,"E6.7.0.1"),sQuery(id+"F5.wireOp",EDGE,"E6.7.0.2"),sQuery(id+"F5.wireOp",EDGE,"E6.7.0.3")])],"isStart":false}),makeQuery(id+"F8.opExtrude","CAP_FACE",FACE,{"disambiguationData":[OSD([sQuery(id+"F5.wireOp",EDGE,"E6.8.0.0"),sQuery(id+"F5.wireOp",EDGE,"E6.8.0.1"),sQuery(id+"F5.wireOp",EDGE,"E6.8.0.2"),sQuery(id+"F5.wireOp",EDGE,"E6.8.0.3")])],"isStart":false})]}),makeQuery(id+"F12.opExtrude","SWEPT_FACE",FACE,{"disambiguationData":[OSD([sQuery(id+"F11.wireOp",EDGE,"E10.4.0.0")])]})]});
            var Q14;
            Q14=makeQuery(id+"F12.boolean.opBoolean","INTERSECT",EDGE,{"derivedFrom":[makeQuery(id+"F8.boolean.opBoolean","MERGE",FACE,{"derivedFrom":[makeQuery(id+"F4.boolean.opBoolean","COPY",FACE,{"derivedFrom":makeQuery(id+"F4.opExtrude","CAP_FACE",FACE,{"disambiguationData":[OSD([sQuery(id+"F3.wireOp",EDGE,"E2.bottom"),sQuery(id+"F3.wireOp",EDGE,"E2.top"),sQuery(id+"F3.wireOp",EDGE,"E2.left"),sQuery(id+"F3.wireOp",EDGE,"E2.right")])],"isStart":false})}),makeQuery(id+"F4.boolean.opBoolean","COPY",FACE,{"derivedFrom":makeQuery(id+"F4.opExtrude","CAP_FACE",FACE,{"disambiguationData":[OSD([sQuery(id+"F3.wireOp",EDGE,"E3.bottom"),sQuery(id+"F3.wireOp",EDGE,"E3.top"),sQuery(id+"F3.wireOp",EDGE,"E3.left"),sQuery(id+"F3.wireOp",EDGE,"E3.right")])],"isStart":false})}),makeQuery(id+"F8.opExtrude","CAP_FACE",FACE,{"disambiguationData":[OSD([sQuery(id+"F5.wireOp",EDGE,"E5.bottom"),sQuery(id+"F5.wireOp",EDGE,"E5.top"),sQuery(id+"F5.wireOp",EDGE,"E5.left"),sQuery(id+"F5.wireOp",EDGE,"E5.right")])],"isStart":false}),makeQuery(id+"F8.opExtrude","CAP_FACE",FACE,{"disambiguationData":[OSD([sQuery(id+"F5.wireOp",EDGE,"E6.1.0.0"),sQuery(id+"F5.wireOp",EDGE,"E6.1.0.1"),sQuery(id+"F5.wireOp",EDGE,"E6.1.0.2"),sQuery(id+"F5.wireOp",EDGE,"E6.1.0.3")])],"isStart":false}),makeQuery(id+"F8.opExtrude","CAP_FACE",FACE,{"disambiguationData":[OSD([sQuery(id+"F5.wireOp",EDGE,"E6.2.0.0"),sQuery(id+"F5.wireOp",EDGE,"E6.2.0.1"),sQuery(id+"F5.wireOp",EDGE,"E6.2.0.2"),sQuery(id+"F5.wireOp",EDGE,"E6.2.0.3")])],"isStart":false}),makeQuery(id+"F8.opExtrude","CAP_FACE",FACE,{"disambiguationData":[OSD([sQuery(id+"F5.wireOp",EDGE,"E6.3.0.0"),sQuery(id+"F5.wireOp",EDGE,"E6.3.0.1"),sQuery(id+"F5.wireOp",EDGE,"E6.3.0.2"),sQuery(id+"F5.wireOp",EDGE,"E6.3.0.3")])],"isStart":false}),makeQuery(id+"F8.opExtrude","CAP_FACE",FACE,{"disambiguationData":[OSD([sQuery(id+"F5.wireOp",EDGE,"E6.4.0.0"),sQuery(id+"F5.wireOp",EDGE,"E6.4.0.1"),sQuery(id+"F5.wireOp",EDGE,"E6.4.0.2"),sQuery(id+"F5.wireOp",EDGE,"E6.4.0.3")])],"isStart":false}),makeQuery(id+"F8.opExtrude","CAP_FACE",FACE,{"disambiguationData":[OSD([sQuery(id+"F5.wireOp",EDGE,"E6.5.0.0"),sQuery(id+"F5.wireOp",EDGE,"E6.5.0.1"),sQuery(id+"F5.wireOp",EDGE,"E6.5.0.2"),sQuery(id+"F5.wireOp",EDGE,"E6.5.0.3")])],"isStart":false}),makeQuery(id+"F8.opExtrude","CAP_FACE",FACE,{"disambiguationData":[OSD([sQuery(id+"F5.wireOp",EDGE,"E6.6.0.0"),sQuery(id+"F5.wireOp",EDGE,"E6.6.0.1"),sQuery(id+"F5.wireOp",EDGE,"E6.6.0.2"),sQuery(id+"F5.wireOp",EDGE,"E6.6.0.3")])],"isStart":false}),makeQuery(id+"F8.opExtrude","CAP_FACE",FACE,{"disambiguationData":[OSD([sQuery(id+"F5.wireOp",EDGE,"E6.7.0.0"),sQuery(id+"F5.wireOp",EDGE,"E6.7.0.1"),sQuery(id+"F5.wireOp",EDGE,"E6.7.0.2"),sQuery(id+"F5.wireOp",EDGE,"E6.7.0.3")])],"isStart":false}),makeQuery(id+"F8.opExtrude","CAP_FACE",FACE,{"disambiguationData":[OSD([sQuery(id+"F5.wireOp",EDGE,"E6.8.0.0"),sQuery(id+"F5.wireOp",EDGE,"E6.8.0.1"),sQuery(id+"F5.wireOp",EDGE,"E6.8.0.2"),sQuery(id+"F5.wireOp",EDGE,"E6.8.0.3")])],"isStart":false})]}),makeQuery(id+"F12.opExtrude","SWEPT_FACE",FACE,{"disambiguationData":[OSD([sQuery(id+"F11.wireOp",EDGE,"E10.5.0.0")])]})]});
            var Q15;
            Q15=makeQuery(id+"F12.boolean.opBoolean","INTERSECT",EDGE,{"derivedFrom":[makeQuery(id+"F8.boolean.opBoolean","MERGE",FACE,{"derivedFrom":[makeQuery(id+"F4.boolean.opBoolean","COPY",FACE,{"derivedFrom":makeQuery(id+"F4.opExtrude","CAP_FACE",FACE,{"disambiguationData":[OSD([sQuery(id+"F3.wireOp",EDGE,"E2.bottom"),sQuery(id+"F3.wireOp",EDGE,"E2.top"),sQuery(id+"F3.wireOp",EDGE,"E2.left"),sQuery(id+"F3.wireOp",EDGE,"E2.right")])],"isStart":false})}),makeQuery(id+"F4.boolean.opBoolean","COPY",FACE,{"derivedFrom":makeQuery(id+"F4.opExtrude","CAP_FACE",FACE,{"disambiguationData":[OSD([sQuery(id+"F3.wireOp",EDGE,"E3.bottom"),sQuery(id+"F3.wireOp",EDGE,"E3.top"),sQuery(id+"F3.wireOp",EDGE,"E3.left"),sQuery(id+"F3.wireOp",EDGE,"E3.right")])],"isStart":false})}),makeQuery(id+"F8.opExtrude","CAP_FACE",FACE,{"disambiguationData":[OSD([sQuery(id+"F5.wireOp",EDGE,"E5.bottom"),sQuery(id+"F5.wireOp",EDGE,"E5.top"),sQuery(id+"F5.wireOp",EDGE,"E5.left"),sQuery(id+"F5.wireOp",EDGE,"E5.right")])],"isStart":false}),makeQuery(id+"F8.opExtrude","CAP_FACE",FACE,{"disambiguationData":[OSD([sQuery(id+"F5.wireOp",EDGE,"E6.1.0.0"),sQuery(id+"F5.wireOp",EDGE,"E6.1.0.1"),sQuery(id+"F5.wireOp",EDGE,"E6.1.0.2"),sQuery(id+"F5.wireOp",EDGE,"E6.1.0.3")])],"isStart":false}),makeQuery(id+"F8.opExtrude","CAP_FACE",FACE,{"disambiguationData":[OSD([sQuery(id+"F5.wireOp",EDGE,"E6.2.0.0"),sQuery(id+"F5.wireOp",EDGE,"E6.2.0.1"),sQuery(id+"F5.wireOp",EDGE,"E6.2.0.2"),sQuery(id+"F5.wireOp",EDGE,"E6.2.0.3")])],"isStart":false}),makeQuery(id+"F8.opExtrude","CAP_FACE",FACE,{"disambiguationData":[OSD([sQuery(id+"F5.wireOp",EDGE,"E6.3.0.0"),sQuery(id+"F5.wireOp",EDGE,"E6.3.0.1"),sQuery(id+"F5.wireOp",EDGE,"E6.3.0.2"),sQuery(id+"F5.wireOp",EDGE,"E6.3.0.3")])],"isStart":false}),makeQuery(id+"F8.opExtrude","CAP_FACE",FACE,{"disambiguationData":[OSD([sQuery(id+"F5.wireOp",EDGE,"E6.4.0.0"),sQuery(id+"F5.wireOp",EDGE,"E6.4.0.1"),sQuery(id+"F5.wireOp",EDGE,"E6.4.0.2"),sQuery(id+"F5.wireOp",EDGE,"E6.4.0.3")])],"isStart":false}),makeQuery(id+"F8.opExtrude","CAP_FACE",FACE,{"disambiguationData":[OSD([sQuery(id+"F5.wireOp",EDGE,"E6.5.0.0"),sQuery(id+"F5.wireOp",EDGE,"E6.5.0.1"),sQuery(id+"F5.wireOp",EDGE,"E6.5.0.2"),sQuery(id+"F5.wireOp",EDGE,"E6.5.0.3")])],"isStart":false}),makeQuery(id+"F8.opExtrude","CAP_FACE",FACE,{"disambiguationData":[OSD([sQuery(id+"F5.wireOp",EDGE,"E6.6.0.0"),sQuery(id+"F5.wireOp",EDGE,"E6.6.0.1"),sQuery(id+"F5.wireOp",EDGE,"E6.6.0.2"),sQuery(id+"F5.wireOp",EDGE,"E6.6.0.3")])],"isStart":false}),makeQuery(id+"F8.opExtrude","CAP_FACE",FACE,{"disambiguationData":[OSD([sQuery(id+"F5.wireOp",EDGE,"E6.7.0.0"),sQuery(id+"F5.wireOp",EDGE,"E6.7.0.1"),sQuery(id+"F5.wireOp",EDGE,"E6.7.0.2"),sQuery(id+"F5.wireOp",EDGE,"E6.7.0.3")])],"isStart":false}),makeQuery(id+"F8.opExtrude","CAP_FACE",FACE,{"disambiguationData":[OSD([sQuery(id+"F5.wireOp",EDGE,"E6.8.0.0"),sQuery(id+"F5.wireOp",EDGE,"E6.8.0.1"),sQuery(id+"F5.wireOp",EDGE,"E6.8.0.2"),sQuery(id+"F5.wireOp",EDGE,"E6.8.0.3")])],"isStart":false})]}),makeQuery(id+"F12.opExtrude","SWEPT_FACE",FACE,{"disambiguationData":[OSD([sQuery(id+"F11.wireOp",EDGE,"E10.6.0.0")])]})]});
            var Q16;
            Q16=makeQuery(id+"F12.boolean.opBoolean","INTERSECT",EDGE,{"derivedFrom":[makeQuery(id+"F8.boolean.opBoolean","MERGE",FACE,{"derivedFrom":[makeQuery(id+"F4.boolean.opBoolean","COPY",FACE,{"derivedFrom":makeQuery(id+"F4.opExtrude","CAP_FACE",FACE,{"disambiguationData":[OSD([sQuery(id+"F3.wireOp",EDGE,"E2.bottom"),sQuery(id+"F3.wireOp",EDGE,"E2.top"),sQuery(id+"F3.wireOp",EDGE,"E2.left"),sQuery(id+"F3.wireOp",EDGE,"E2.right")])],"isStart":false})}),makeQuery(id+"F4.boolean.opBoolean","COPY",FACE,{"derivedFrom":makeQuery(id+"F4.opExtrude","CAP_FACE",FACE,{"disambiguationData":[OSD([sQuery(id+"F3.wireOp",EDGE,"E3.bottom"),sQuery(id+"F3.wireOp",EDGE,"E3.top"),sQuery(id+"F3.wireOp",EDGE,"E3.left"),sQuery(id+"F3.wireOp",EDGE,"E3.right")])],"isStart":false})}),makeQuery(id+"F8.opExtrude","CAP_FACE",FACE,{"disambiguationData":[OSD([sQuery(id+"F5.wireOp",EDGE,"E5.bottom"),sQuery(id+"F5.wireOp",EDGE,"E5.top"),sQuery(id+"F5.wireOp",EDGE,"E5.left"),sQuery(id+"F5.wireOp",EDGE,"E5.right")])],"isStart":false}),makeQuery(id+"F8.opExtrude","CAP_FACE",FACE,{"disambiguationData":[OSD([sQuery(id+"F5.wireOp",EDGE,"E6.1.0.0"),sQuery(id+"F5.wireOp",EDGE,"E6.1.0.1"),sQuery(id+"F5.wireOp",EDGE,"E6.1.0.2"),sQuery(id+"F5.wireOp",EDGE,"E6.1.0.3")])],"isStart":false}),makeQuery(id+"F8.opExtrude","CAP_FACE",FACE,{"disambiguationData":[OSD([sQuery(id+"F5.wireOp",EDGE,"E6.2.0.0"),sQuery(id+"F5.wireOp",EDGE,"E6.2.0.1"),sQuery(id+"F5.wireOp",EDGE,"E6.2.0.2"),sQuery(id+"F5.wireOp",EDGE,"E6.2.0.3")])],"isStart":false}),makeQuery(id+"F8.opExtrude","CAP_FACE",FACE,{"disambiguationData":[OSD([sQuery(id+"F5.wireOp",EDGE,"E6.3.0.0"),sQuery(id+"F5.wireOp",EDGE,"E6.3.0.1"),sQuery(id+"F5.wireOp",EDGE,"E6.3.0.2"),sQuery(id+"F5.wireOp",EDGE,"E6.3.0.3")])],"isStart":false}),makeQuery(id+"F8.opExtrude","CAP_FACE",FACE,{"disambiguationData":[OSD([sQuery(id+"F5.wireOp",EDGE,"E6.4.0.0"),sQuery(id+"F5.wireOp",EDGE,"E6.4.0.1"),sQuery(id+"F5.wireOp",EDGE,"E6.4.0.2"),sQuery(id+"F5.wireOp",EDGE,"E6.4.0.3")])],"isStart":false}),makeQuery(id+"F8.opExtrude","CAP_FACE",FACE,{"disambiguationData":[OSD([sQuery(id+"F5.wireOp",EDGE,"E6.5.0.0"),sQuery(id+"F5.wireOp",EDGE,"E6.5.0.1"),sQuery(id+"F5.wireOp",EDGE,"E6.5.0.2"),sQuery(id+"F5.wireOp",EDGE,"E6.5.0.3")])],"isStart":false}),makeQuery(id+"F8.opExtrude","CAP_FACE",FACE,{"disambiguationData":[OSD([sQuery(id+"F5.wireOp",EDGE,"E6.6.0.0"),sQuery(id+"F5.wireOp",EDGE,"E6.6.0.1"),sQuery(id+"F5.wireOp",EDGE,"E6.6.0.2"),sQuery(id+"F5.wireOp",EDGE,"E6.6.0.3")])],"isStart":false}),makeQuery(id+"F8.opExtrude","CAP_FACE",FACE,{"disambiguationData":[OSD([sQuery(id+"F5.wireOp",EDGE,"E6.7.0.0"),sQuery(id+"F5.wireOp",EDGE,"E6.7.0.1"),sQuery(id+"F5.wireOp",EDGE,"E6.7.0.2"),sQuery(id+"F5.wireOp",EDGE,"E6.7.0.3")])],"isStart":false}),makeQuery(id+"F8.opExtrude","CAP_FACE",FACE,{"disambiguationData":[OSD([sQuery(id+"F5.wireOp",EDGE,"E6.8.0.0"),sQuery(id+"F5.wireOp",EDGE,"E6.8.0.1"),sQuery(id+"F5.wireOp",EDGE,"E6.8.0.2"),sQuery(id+"F5.wireOp",EDGE,"E6.8.0.3")])],"isStart":false})]}),makeQuery(id+"F12.opExtrude","SWEPT_FACE",FACE,{"disambiguationData":[OSD([sQuery(id+"F11.wireOp",EDGE,"E10.7.0.0")])]})]});
            var Q17;
            Q17=makeQuery(id+"F12.boolean.opBoolean","INTERSECT",EDGE,{"derivedFrom":[makeQuery(id+"F8.boolean.opBoolean","MERGE",FACE,{"derivedFrom":[makeQuery(id+"F4.boolean.opBoolean","COPY",FACE,{"derivedFrom":makeQuery(id+"F4.opExtrude","CAP_FACE",FACE,{"disambiguationData":[OSD([sQuery(id+"F3.wireOp",EDGE,"E2.bottom"),sQuery(id+"F3.wireOp",EDGE,"E2.top"),sQuery(id+"F3.wireOp",EDGE,"E2.left"),sQuery(id+"F3.wireOp",EDGE,"E2.right")])],"isStart":false})}),makeQuery(id+"F4.boolean.opBoolean","COPY",FACE,{"derivedFrom":makeQuery(id+"F4.opExtrude","CAP_FACE",FACE,{"disambiguationData":[OSD([sQuery(id+"F3.wireOp",EDGE,"E3.bottom"),sQuery(id+"F3.wireOp",EDGE,"E3.top"),sQuery(id+"F3.wireOp",EDGE,"E3.left"),sQuery(id+"F3.wireOp",EDGE,"E3.right")])],"isStart":false})}),makeQuery(id+"F8.opExtrude","CAP_FACE",FACE,{"disambiguationData":[OSD([sQuery(id+"F5.wireOp",EDGE,"E5.bottom"),sQuery(id+"F5.wireOp",EDGE,"E5.top"),sQuery(id+"F5.wireOp",EDGE,"E5.left"),sQuery(id+"F5.wireOp",EDGE,"E5.right")])],"isStart":false}),makeQuery(id+"F8.opExtrude","CAP_FACE",FACE,{"disambiguationData":[OSD([sQuery(id+"F5.wireOp",EDGE,"E6.1.0.0"),sQuery(id+"F5.wireOp",EDGE,"E6.1.0.1"),sQuery(id+"F5.wireOp",EDGE,"E6.1.0.2"),sQuery(id+"F5.wireOp",EDGE,"E6.1.0.3")])],"isStart":false}),makeQuery(id+"F8.opExtrude","CAP_FACE",FACE,{"disambiguationData":[OSD([sQuery(id+"F5.wireOp",EDGE,"E6.2.0.0"),sQuery(id+"F5.wireOp",EDGE,"E6.2.0.1"),sQuery(id+"F5.wireOp",EDGE,"E6.2.0.2"),sQuery(id+"F5.wireOp",EDGE,"E6.2.0.3")])],"isStart":false}),makeQuery(id+"F8.opExtrude","CAP_FACE",FACE,{"disambiguationData":[OSD([sQuery(id+"F5.wireOp",EDGE,"E6.3.0.0"),sQuery(id+"F5.wireOp",EDGE,"E6.3.0.1"),sQuery(id+"F5.wireOp",EDGE,"E6.3.0.2"),sQuery(id+"F5.wireOp",EDGE,"E6.3.0.3")])],"isStart":false}),makeQuery(id+"F8.opExtrude","CAP_FACE",FACE,{"disambiguationData":[OSD([sQuery(id+"F5.wireOp",EDGE,"E6.4.0.0"),sQuery(id+"F5.wireOp",EDGE,"E6.4.0.1"),sQuery(id+"F5.wireOp",EDGE,"E6.4.0.2"),sQuery(id+"F5.wireOp",EDGE,"E6.4.0.3")])],"isStart":false}),makeQuery(id+"F8.opExtrude","CAP_FACE",FACE,{"disambiguationData":[OSD([sQuery(id+"F5.wireOp",EDGE,"E6.5.0.0"),sQuery(id+"F5.wireOp",EDGE,"E6.5.0.1"),sQuery(id+"F5.wireOp",EDGE,"E6.5.0.2"),sQuery(id+"F5.wireOp",EDGE,"E6.5.0.3")])],"isStart":false}),makeQuery(id+"F8.opExtrude","CAP_FACE",FACE,{"disambiguationData":[OSD([sQuery(id+"F5.wireOp",EDGE,"E6.6.0.0"),sQuery(id+"F5.wireOp",EDGE,"E6.6.0.1"),sQuery(id+"F5.wireOp",EDGE,"E6.6.0.2"),sQuery(id+"F5.wireOp",EDGE,"E6.6.0.3")])],"isStart":false}),makeQuery(id+"F8.opExtrude","CAP_FACE",FACE,{"disambiguationData":[OSD([sQuery(id+"F5.wireOp",EDGE,"E6.7.0.0"),sQuery(id+"F5.wireOp",EDGE,"E6.7.0.1"),sQuery(id+"F5.wireOp",EDGE,"E6.7.0.2"),sQuery(id+"F5.wireOp",EDGE,"E6.7.0.3")])],"isStart":false}),makeQuery(id+"F8.opExtrude","CAP_FACE",FACE,{"disambiguationData":[OSD([sQuery(id+"F5.wireOp",EDGE,"E6.8.0.0"),sQuery(id+"F5.wireOp",EDGE,"E6.8.0.1"),sQuery(id+"F5.wireOp",EDGE,"E6.8.0.2"),sQuery(id+"F5.wireOp",EDGE,"E6.8.0.3")])],"isStart":false})]}),makeQuery(id+"F12.opExtrude","SWEPT_FACE",FACE,{"disambiguationData":[OSD([sQuery(id+"F11.wireOp",EDGE,"E10.8.0.0")])]})]});
            fillet(context, id + "F13", {"entities" : qUnion([Q0, Q1, Q2, Q3, Q4, Q5, Q6, Q7, Q8, Q9, Q10, Q11, Q12, Q13, Q14, Q15, Q16, Q17]), "radius" : 1 * mm, "tangentPropagation" : true, "allowEdgeOverflow" : false});
        }
        {
            var Q0;
            Q0=qCreatedBy(makeId("Front.planeOp"),FACE);
            var sketch = newSketch(context, id + "F14", { "sketchPlane" : qUnion([Q0])});
            skLineSegment(sketch, "E21", {"start": v(-44.5, 5) * mm, "end": v(-44.5, 20) * mm});
            skLineSegment(sketch, "E22", {"start": v(-44.5, 20) * mm, "end": v(44.5, 20) * mm});
            skLineSegment(sketch, "E23", {"start": v(44.5, 20) * mm, "end": v(44.5, 5) * mm});
            skLineSegment(sketch, "E24", {"start": v(44.5, 5) * mm, "end": v(46.5, 5) * mm});
            skLineSegment(sketch, "E25", {"start": v(46.5, 5) * mm, "end": v(46.5, 22) * mm});
            skLineSegment(sketch, "E26", {"start": v(46.5, 22) * mm, "end": v(-46.5, 22) * mm});
            skLineSegment(sketch, "E27", {"start": v(-46.5, 22) * mm, "end": v(-46.5, 5) * mm});
            skLineSegment(sketch, "E28", {"start": v(-46.5, 5) * mm, "end": v(-44.5, 5) * mm});
            skSolve(sketch);
        }
        {
            var Q0;
            Q0 = qSketchRegion(id + "F14", true);
            extrude(context, id + "F15", {"entities" : qUnion([Q0]), "depth" : 20 * mm, "hasSecondDirection" : true, "secondDirectionOppositeDirection" : true, "secondDirectionDepth" : 20 * mm});
        }
        {
            var Q0;
            Q0=makeQuery(id+"F15.opExtrude","SWEPT_FACE",FACE,{"disambiguationData":[OSD([sQuery(id+"F14.wireOp",EDGE,"E27")])]});
            var sketch = newSketch(context, id + "F16", { "sketchPlane" : qUnion([Q0])});
            skLineSegment(sketch, "E29", {"start": v(-20, 8.59) * mm, "end": v(-10, 22) * mm});
            skLineSegment(sketch, "E30", {"start": v(10, 22) * mm, "end": v(20, 8.59) * mm});
            skLineSegment(sketch, "E31", {"start": v(20, 8.59) * mm, "end": v(15.19, 5) * mm});
            skLineSegment(sketch, "E32", {"start": v(15.19, 5) * mm, "end": v(6.99, 16) * mm});
            skLineSegment(sketch, "E33", {"start": v(6.99, 16) * mm, "end": v(-6.99, 16) * mm});
            skLineSegment(sketch, "E34", {"start": v(-6.99, 16) * mm, "end": v(-15.19, 5) * mm});
            skLineSegment(sketch, "E35", {"start": v(-15.19, 5) * mm, "end": v(-20, 8.59) * mm});
            skLineSegment(sketch, "E36", {"start": v(-10, 22) * mm, "end": v(-22.88, 22) * mm});
            skLineSegment(sketch, "E37", {"start": v(-22.88, 22) * mm, "end": v(-22.88, 3.64) * mm});
            skLineSegment(sketch, "E38", {"start": v(-22.88, 3.64) * mm, "end": v(22.96, 3.64) * mm});
            skLineSegment(sketch, "E39", {"start": v(22.96, 3.64) * mm, "end": v(22.96, 22) * mm});
            skLineSegment(sketch, "E40", {"start": v(22.96, 22) * mm, "end": v(10, 22) * mm});
            skSolve(sketch);
        }
        {
            var Q0;
            Q0 = qSketchRegion(id + "F16", true);
            extrude(context, id + "F17", {"entities" : qUnion([Q0]), "operationType" : NewBodyOperationType.REMOVE, "oppositeDirection" : true, "depth" : 110 * mm});
        }
        {
            var Q0;
            {var subQ0=sQuery(id+"F14.wireOp",EDGE,"E27");var subQ1=sQuery(id+"F16.wireOp",EDGE,"E35");var subQ2=sQuery(id+"F16.wireOp",EDGE,"E29");Q0=makeQuery(id+"F17.boolean.opBoolean","COPY",EDGE,{"disambiguationData":[TD([makeQuery(id+"F15.opExtrude","SWEPT_FACE",FACE,{"disambiguationData":[OSD([sQuery(id+"F14.wireOp",EDGE,"E21")])]})])],"derivedFrom":makeQuery(id+"F17.opExtrude","SWEPT_EDGE",EDGE,{"disambiguationData":[OSD([subQ0,subQ2,subQ1])]})});}
            var Q1;
            {var subQ0=sQuery(id+"F14.wireOp",EDGE,"E27");var subQ1=sQuery(id+"F16.wireOp",EDGE,"E35");var subQ2=sQuery(id+"F16.wireOp",EDGE,"E34");Q1=makeQuery(id+"F17.boolean.opBoolean","COPY",EDGE,{"disambiguationData":[TD([makeQuery(id+"F15.opExtrude","SWEPT_FACE",FACE,{"disambiguationData":[OSD([sQuery(id+"F14.wireOp",EDGE,"E21")])]})])],"derivedFrom":makeQuery(id+"F17.opExtrude","SWEPT_EDGE",EDGE,{"disambiguationData":[OSD([subQ0,sQuery(id+"F14.wireOp",EDGE,"E28"),subQ2,subQ1])]})});}
            var Q2;
            {var subQ0=sQuery(id+"F14.wireOp",EDGE,"E27");var subQ1=sQuery(id+"F16.wireOp",EDGE,"E31");var subQ2=sQuery(id+"F16.wireOp",EDGE,"E32");Q2=makeQuery(id+"F17.boolean.opBoolean","COPY",EDGE,{"disambiguationData":[TD([makeQuery(id+"F15.opExtrude","SWEPT_FACE",FACE,{"disambiguationData":[OSD([sQuery(id+"F14.wireOp",EDGE,"E21")])]})])],"derivedFrom":makeQuery(id+"F17.opExtrude","SWEPT_EDGE",EDGE,{"disambiguationData":[OSD([subQ0,sQuery(id+"F14.wireOp",EDGE,"E28"),subQ1,subQ2])]})});}
            var Q3;
            {var subQ0=sQuery(id+"F14.wireOp",EDGE,"E27");var subQ1=sQuery(id+"F16.wireOp",EDGE,"E30");var subQ2=sQuery(id+"F16.wireOp",EDGE,"E31");Q3=makeQuery(id+"F17.boolean.opBoolean","COPY",EDGE,{"disambiguationData":[TD([makeQuery(id+"F15.opExtrude","SWEPT_FACE",FACE,{"disambiguationData":[OSD([sQuery(id+"F14.wireOp",EDGE,"E21")])]})])],"derivedFrom":makeQuery(id+"F17.opExtrude","SWEPT_EDGE",EDGE,{"disambiguationData":[OSD([subQ0,subQ1,subQ2])]})});}
            var Q4;
            {var subQ0=sQuery(id+"F16.wireOp",EDGE,"E30");var subQ1=sQuery(id+"F16.wireOp",EDGE,"E31");Q4=makeQuery(id+"F17.boolean.opBoolean","COPY",EDGE,{"disambiguationData":[TD([makeQuery(id+"F15.opExtrude","SWEPT_FACE",FACE,{"disambiguationData":[OSD([sQuery(id+"F14.wireOp",EDGE,"E23")])]})])],"derivedFrom":makeQuery(id+"F17.opExtrude","SWEPT_EDGE",EDGE,{"disambiguationData":[OSD([sQuery(id+"F14.wireOp",EDGE,"E27"),subQ0,subQ1])]})});}
            var Q5;
            {var subQ0=sQuery(id+"F16.wireOp",EDGE,"E31");var subQ1=sQuery(id+"F16.wireOp",EDGE,"E32");Q5=makeQuery(id+"F17.boolean.opBoolean","COPY",EDGE,{"disambiguationData":[TD([makeQuery(id+"F15.opExtrude","SWEPT_FACE",FACE,{"disambiguationData":[OSD([sQuery(id+"F14.wireOp",EDGE,"E23")])]})])],"derivedFrom":makeQuery(id+"F17.opExtrude","SWEPT_EDGE",EDGE,{"disambiguationData":[OSD([sQuery(id+"F14.wireOp",EDGE,"E27"),sQuery(id+"F14.wireOp",EDGE,"E28"),subQ0,subQ1])]})});}
            var Q6;
            {var subQ0=sQuery(id+"F16.wireOp",EDGE,"E35");var subQ1=sQuery(id+"F16.wireOp",EDGE,"E34");Q6=makeQuery(id+"F17.boolean.opBoolean","COPY",EDGE,{"disambiguationData":[TD([makeQuery(id+"F15.opExtrude","SWEPT_FACE",FACE,{"disambiguationData":[OSD([sQuery(id+"F14.wireOp",EDGE,"E23")])]})])],"derivedFrom":makeQuery(id+"F17.opExtrude","SWEPT_EDGE",EDGE,{"disambiguationData":[OSD([sQuery(id+"F14.wireOp",EDGE,"E27"),sQuery(id+"F14.wireOp",EDGE,"E28"),subQ1,subQ0])]})});}
            var Q7;
            {var subQ0=sQuery(id+"F16.wireOp",EDGE,"E35");var subQ1=sQuery(id+"F16.wireOp",EDGE,"E29");Q7=makeQuery(id+"F17.boolean.opBoolean","COPY",EDGE,{"disambiguationData":[TD([makeQuery(id+"F15.opExtrude","SWEPT_FACE",FACE,{"disambiguationData":[OSD([sQuery(id+"F14.wireOp",EDGE,"E23")])]})])],"derivedFrom":makeQuery(id+"F17.opExtrude","SWEPT_EDGE",EDGE,{"disambiguationData":[OSD([sQuery(id+"F14.wireOp",EDGE,"E27"),subQ1,subQ0])]})});}
            var Q8;
            Q8=makeQuery(id+"F17.boolean.opBoolean","COPY",EDGE,{"derivedFrom":makeQuery(id+"F17.opExtrude","SWEPT_EDGE",EDGE,{"disambiguationData":[OSD([sQuery(id+"F14.wireOp",EDGE,"E26"),sQuery(id+"F14.wireOp",EDGE,"E27"),sQuery(id+"F16.wireOp",EDGE,"E29"),sQuery(id+"F16.wireOp",EDGE,"E36")])]})});
            var Q9;
            {var subQ0=sQuery(id+"F16.wireOp",EDGE,"E32");var subQ1=sQuery(id+"F16.wireOp",EDGE,"E33");Q9=makeQuery(id+"F17.boolean.opBoolean","COPY",EDGE,{"disambiguationData":[TD([makeQuery(id+"F15.opExtrude","SWEPT_FACE",FACE,{"disambiguationData":[OSD([sQuery(id+"F14.wireOp",EDGE,"E23")])]})])],"derivedFrom":makeQuery(id+"F17.opExtrude","SWEPT_EDGE",EDGE,{"disambiguationData":[OSD([subQ0,subQ1])]})});}
            var Q10;
            {var subQ0=sQuery(id+"F16.wireOp",EDGE,"E33");var subQ1=sQuery(id+"F16.wireOp",EDGE,"E34");Q10=makeQuery(id+"F17.boolean.opBoolean","COPY",EDGE,{"disambiguationData":[TD([makeQuery(id+"F15.opExtrude","SWEPT_FACE",FACE,{"disambiguationData":[OSD([sQuery(id+"F14.wireOp",EDGE,"E23")])]})])],"derivedFrom":makeQuery(id+"F17.opExtrude","SWEPT_EDGE",EDGE,{"disambiguationData":[OSD([subQ0,subQ1])]})});}
            var Q11;
            Q11=makeQuery(id+"F17.boolean.opBoolean","COPY",EDGE,{"derivedFrom":makeQuery(id+"F17.opExtrude","SWEPT_EDGE",EDGE,{"disambiguationData":[OSD([sQuery(id+"F14.wireOp",EDGE,"E26"),sQuery(id+"F14.wireOp",EDGE,"E27"),sQuery(id+"F16.wireOp",EDGE,"E30"),sQuery(id+"F16.wireOp",EDGE,"E40")])]})});
            var Q12;
            {var subQ0=sQuery(id+"F16.wireOp",EDGE,"E33");var subQ1=sQuery(id+"F16.wireOp",EDGE,"E34");Q12=makeQuery(id+"F17.boolean.opBoolean","COPY",EDGE,{"disambiguationData":[TD([makeQuery(id+"F15.opExtrude","SWEPT_FACE",FACE,{"disambiguationData":[OSD([sQuery(id+"F14.wireOp",EDGE,"E21")])]})])],"derivedFrom":makeQuery(id+"F17.opExtrude","SWEPT_EDGE",EDGE,{"disambiguationData":[OSD([subQ0,subQ1])]})});}
            var Q13;
            {var subQ0=sQuery(id+"F16.wireOp",EDGE,"E32");var subQ1=sQuery(id+"F16.wireOp",EDGE,"E33");Q13=makeQuery(id+"F17.boolean.opBoolean","COPY",EDGE,{"disambiguationData":[TD([makeQuery(id+"F15.opExtrude","SWEPT_FACE",FACE,{"disambiguationData":[OSD([sQuery(id+"F14.wireOp",EDGE,"E21")])]})])],"derivedFrom":makeQuery(id+"F17.opExtrude","SWEPT_EDGE",EDGE,{"disambiguationData":[OSD([subQ0,subQ1])]})});}
            fillet(context, id + "F18", {"entities" : qUnion([Q0, Q1, Q2, Q3, Q4, Q5, Q6, Q7, Q8, Q9, Q10, Q11, Q12, Q13]), "radius" : 2.5 * mm, "tangentPropagation" : true, "allowEdgeOverflow" : false});
        }
        {
            var Q0;
            Q0=makeQuery(id+"F15.opExtrude","SWEPT_EDGE",EDGE,{"disambiguationData":[OSD([sQuery(id+"F14.wireOp",EDGE,"E26"),sQuery(id+"F14.wireOp",EDGE,"E27")])]});
            var Q1;
            Q1=makeQuery(id+"F15.opExtrude","SWEPT_EDGE",EDGE,{"disambiguationData":[OSD([sQuery(id+"F14.wireOp",EDGE,"E25"),sQuery(id+"F14.wireOp",EDGE,"E26")])]});
            fillet(context, id + "F19", {"entities" : qUnion([Q0, Q1]), "radius" : 1 * mm, "tangentPropagation" : true, "allowEdgeOverflow" : false});
        }
        {
            var Q0;
            Q0=makeQuery(id+"F15.opExtrude","SWEPT_EDGE",EDGE,{"disambiguationData":[OSD([sQuery(id+"F14.wireOp",EDGE,"E21"),sQuery(id+"F14.wireOp",EDGE,"E22")])]});
            var Q1;
            Q1=makeQuery(id+"F15.opExtrude","SWEPT_EDGE",EDGE,{"disambiguationData":[OSD([sQuery(id+"F14.wireOp",EDGE,"E22"),sQuery(id+"F14.wireOp",EDGE,"E23")])]});
            fillet(context, id + "F20", {"entities" : qUnion([Q0, Q1]), "radius" : 3 * mm, "tangentPropagation" : true, "allowEdgeOverflow" : false});
        }
        {
            var Q0;
            Q0=makeQuery(id+"F15.opExtrude","SWEPT_FACE",FACE,{"disambiguationData":[OSD([sQuery(id+"F14.wireOp",EDGE,"E27")])]});
            var sketch = newSketch(context, id + "F21", { "sketchPlane" : qUnion([Q0])});
            skCircle(sketch, "E41", {"center": v(16.1, 8.8) * mm, "radius": 1 * mm});
            skLineSegment(sketch, "E42", {"start": v(17, 7.6) * mm, "end": v(16.1, 8.8) * mm});
            skLineSegment(sketch, "E43", {"start": v(0, 0) * mm, "end": v(0, 13.69) * mm, "construction": true});
            skCircle(sketch, "E44.MirrorC", {"center": v(-16.1, 8.8) * mm, "radius": 1 * mm});
            skSolve(sketch);
        }
        {
            var Q0;
            Q0 = qSketchRegion(id + "F21", true);
            extrude(context, id + "F22", {"entities" : qUnion([Q0]), "operationType" : NewBodyOperationType.REMOVE, "oppositeDirection" : true, "depth" : 110 * mm});
        }
        {
            var Q0;
            Q0=makeQuery(id+"F15.opExtrude","SWEPT_FACE",FACE,{"disambiguationData":[OSD([sQuery(id+"F14.wireOp",EDGE,"E27")])]});
            var sketch = newSketch(context, id + "F23", { "sketchPlane" : qUnion([Q0])});
            skCircle(sketch, "E45", {"center": v(-16.1, 8.8) * mm, "radius": 1 * mm});
            skCircle(sketch, "E46", {"center": v(16.1, 8.8) * mm, "radius": 1.01 * mm});
            skSolve(sketch);
        }
        {
            var Q0;
            Q0 = qSketchRegion(id + "F23", true);
            extrude(context, id + "F24", {"entities" : qUnion([Q0]), "operationType" : NewBodyOperationType.ADD, "oppositeDirection" : true, "depth" : 2 * mm});
        }
        {
            var Q0;
            Q0=makeQuery(id+"F23.imprint","IMPRINT",FACE,{"disambiguationData":[TD([[makeQuery(id+"F23.imprint","IMPRINT",EDGE,{"derivedFrom":sQuery(id+"F23.wireOp",EDGE,"E45")}),1.0]])]});
            var sketch = newSketch(context, id + "F25", { "sketchPlane" : qUnion([Q0])});
            skCircle(sketch, "E47", {"center": v(-16.1, 8.8) * mm, "radius": 0.88 * mm});
            skCircle(sketch, "E48", {"center": v(16.1, 8.8) * mm, "radius": 0.88 * mm});
            skSolve(sketch);
        }
        {
            var Q0;
            Q0 = qSketchRegion(id + "F25", true);
            extrude(context, id + "F26", {"entities" : qUnion([Q0]), "operationType" : NewBodyOperationType.ADD, "oppositeDirection" : true, "depth" : 4 * mm});
        }
        {
            var Q0;
            Q0=makeQuery(id+"F15.opExtrude","SWEPT_FACE",FACE,{"disambiguationData":[OSD([sQuery(id+"F14.wireOp",EDGE,"E25")])]});
            var sketch = newSketch(context, id + "F27", { "sketchPlane" : qUnion([Q0])});
            skCircle(sketch, "E49.0", {"center": v(16.1, 8.8) * mm, "radius": 1 * mm});
            skCircle(sketch, "E49.1", {"center": v(-16.1, 8.8) * mm, "radius": 1.01 * mm});
            skSolve(sketch);
        }
        {
            var Q0;
            Q0 = qSketchRegion(id + "F27", true);
            extrude(context, id + "F28", {"entities" : qUnion([Q0]), "operationType" : NewBodyOperationType.ADD, "oppositeDirection" : true, "depth" : 2 * mm});
        }
        {
            var Q0;
            Q0=makeQuery(id+"F28.boolean.opBoolean","MERGE",FACE,{"derivedFrom":[makeQuery(id+"F15.opExtrude","SWEPT_FACE",FACE,{"disambiguationData":[OSD([sQuery(id+"F14.wireOp",EDGE,"E25")])]}),makeQuery(id+"F28.opExtrude","CAP_FACE",FACE,{"disambiguationData":[OSD([sQuery(id+"F27.wireOp",EDGE,"E49.0")])],"isStart":true}),makeQuery(id+"F28.opExtrude","CAP_FACE",FACE,{"disambiguationData":[OSD([sQuery(id+"F27.wireOp",EDGE,"E49.1")])],"isStart":true})]});
            var sketch = newSketch(context, id + "F29", { "sketchPlane" : qUnion([Q0])});
            skCircle(sketch, "E50.0", {"center": v(16.1, 8.8) * mm, "radius": 0.88 * mm});
            skCircle(sketch, "E50.1", {"center": v(-16.1, 8.8) * mm, "radius": 0.88 * mm});
            skSolve(sketch);
        }
        {
            var Q0;
            Q0 = qSketchRegion(id + "F29", true);
            extrude(context, id + "F30", {"entities" : qUnion([Q0]), "operationType" : NewBodyOperationType.ADD, "oppositeDirection" : true, "depth" : 4 * mm});
        }
        {
            var Q0;
            Q0=makeQuery(id+"F26.opExtrude","CAP_FACE",FACE,{"disambiguationData":[OSD([sQuery(id+"F25.wireOp",EDGE,"E47")])],"isStart":false});
            var sketch = newSketch(context, id + "F31", { "sketchPlane" : qUnion([Q0])});
            skCircle(sketch, "E51.0", {"center": v(16.1, 8.8) * mm, "radius": 0.88 * mm});
            skSolve(sketch);
        }
        {
            var Q0;
            Q0 = qSketchRegion(id + "F31", true);
            extrude(context, id + "F32", {"entities" : qUnion([Q0]), "operationType" : NewBodyOperationType.ADD, "depth" : 1.5 * mm});
        }
        {
            var Q0;
            Q0=makeQuery(id+"F30.opExtrude","CAP_FACE",FACE,{"disambiguationData":[OSD([sQuery(id+"F29.wireOp",EDGE,"E50.0")])],"isStart":false});
            var sketch = newSketch(context, id + "F33", { "sketchPlane" : qUnion([Q0])});
            skCircle(sketch, "E52.0", {"center": v(-16.1, 8.8) * mm, "radius": 0.88 * mm});
            skSolve(sketch);
        }
        {
            var Q0;
            Q0 = qSketchRegion(id + "F33", true);
            extrude(context, id + "F34", {"entities" : qUnion([Q0]), "operationType" : NewBodyOperationType.ADD, "depth" : 1.5 * mm});
        }
        {
            var Q0;
            Q0=makeQuery(id+"F20.opFillet","BLEND_EDGE",EDGE,{"blendedFrom":[makeQuery(id+"F15.opExtrude","SWEPT_EDGE",EDGE,{"disambiguationData":[OSD([sQuery(id+"F14.wireOp",EDGE,"E22"),sQuery(id+"F14.wireOp",EDGE,"E23")])]}),makeQuery(id+"F17.boolean.opBoolean","COPY",FACE,{"derivedFrom":makeQuery(id+"F17.opExtrude","SWEPT_FACE",FACE,{"disambiguationData":[OSD([sQuery(id+"F16.wireOp",EDGE,"E29")])]})})],"blendedInto":[makeQuery(id+"F17.boolean.opBoolean","COPY",FACE,{"derivedFrom":makeQuery(id+"F17.opExtrude","SWEPT_FACE",FACE,{"disambiguationData":[OSD([sQuery(id+"F16.wireOp",EDGE,"E29")])]})})]});
            fillet(context, id + "F35", {"entities" : qUnion([Q0]), "radius" : 1 * mm, "tangentPropagation" : true, "allowEdgeOverflow" : false});
        }
    });
